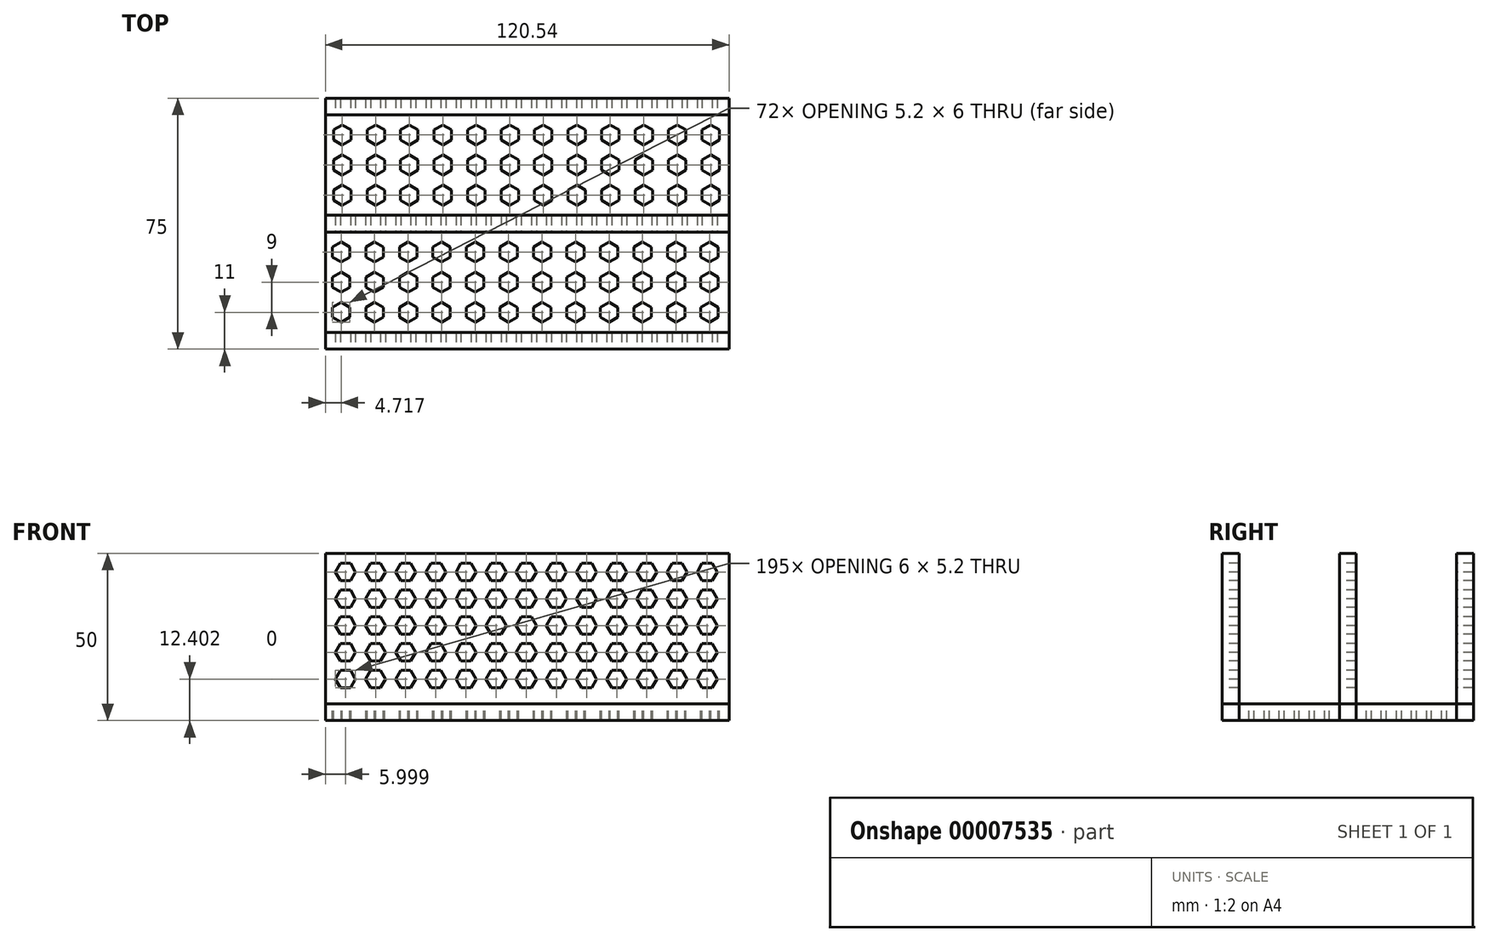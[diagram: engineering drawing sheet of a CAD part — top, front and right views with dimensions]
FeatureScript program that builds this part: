
annotation { "Feature Type Name" : "Feature", "Feature Type Description" : "" }
export const myFeature = defineFeature(function(context is Context, id is Id, definition is map)
    precondition{}
    {
        {
            var Q0;
            Q0=qCreatedBy(makeId("Top.planeOp"),FACE);
            var sketch = newSketch(context, id + "F0", { "sketchPlane" : qUnion([Q0])});
            skLineSegment(sketch, "E0.bottom", {"start": v(-52.44, 35) * mm, "end": v(68.1, 35) * mm});
            skLineSegment(sketch, "E0.top", {"start": v(-52.44, -40) * mm, "end": v(68.1, -40) * mm});
            skLineSegment(sketch, "E0.left", {"start": v(-52.44, 35) * mm, "end": v(-52.44, -40) * mm});
            skLineSegment(sketch, "E0.right", {"start": v(68.1, 35) * mm, "end": v(68.1, -40) * mm});
            skLineSegment(sketch, "E1.top", {"start": v(-52.44, -35) * mm, "end": v(68.1, -35) * mm});
            skLineSegment(sketch, "E1.left", {"start": v(-52.44, -40) * mm, "end": v(-52.44, -35) * mm});
            skLineSegment(sketch, "E1.right", {"start": v(68.1, -40) * mm, "end": v(68.1, -35) * mm});
            skLineSegment(sketch, "E2.bottom", {"start": v(68.1, -5) * mm, "end": v(-52.44, -5) * mm});
            skLineSegment(sketch, "E2.top", {"start": v(68.1, 0) * mm, "end": v(-52.44, 0) * mm});
            skLineSegment(sketch, "E2.left", {"start": v(68.1, -5) * mm, "end": v(68.1, 0) * mm});
            skLineSegment(sketch, "E2.right", {"start": v(-52.44, -5) * mm, "end": v(-52.44, 0) * mm});
            skLineSegment(sketch, "E3.top", {"start": v(-52.44, 30) * mm, "end": v(68.1, 30) * mm});
            skLineSegment(sketch, "E3.left", {"start": v(-52.44, 35) * mm, "end": v(-52.44, 30) * mm});
            skLineSegment(sketch, "E3.right", {"start": v(68.1, 35) * mm, "end": v(68.1, 30) * mm});
            skSolve(sketch);
        }
        {
            var Q0;
            Q0 = qSketchRegion(id + "F0", true);
            extrude(context, id + "F1", {"entities" : qUnion([Q0]), "depth" : 5 * mm});
        }
        {
            var Q0;
            Q0=makeQuery(id+"F0.imprint","IMPRINT",FACE,{"disambiguationData":[TD([[makeQuery(id+"F0.imprint","IMPRINT",EDGE,{"derivedFrom":sQuery(id+"F0.wireOp",EDGE,"E0.top")}),1.0]])]});
            var Q1;
            Q1=makeQuery(id+"F0.imprint","IMPRINT",FACE,{"disambiguationData":[TD([[makeQuery(id+"F0.imprint","IMPRINT",EDGE,{"derivedFrom":sQuery(id+"F0.wireOp",EDGE,"E2.bottom")}),-1.0]])]});
            var Q2;
            Q2=makeQuery(id+"F0.imprint","IMPRINT",FACE,{"disambiguationData":[TD([[makeQuery(id+"F0.imprint","IMPRINT",EDGE,{"derivedFrom":sQuery(id+"F0.wireOp",EDGE,"E0.bottom")}),-1.0]])]});
            extrude(context, id + "F2", {"entities" : qUnion([Q0, Q1, Q2]), "depth" : 50 * mm});
        }
        {
            var Q0;
            Q0=makeQuery(id+"F1.opExtrude","CAP_FACE",FACE,{"disambiguationData":[OSD([sQuery(id+"F0.wireOp",EDGE,"E0.left"),sQuery(id+"F0.wireOp",EDGE,"E0.right"),sQuery(id+"F0.wireOp",EDGE,"E0.top"),sQuery(id+"F0.wireOp",EDGE,"E1.left"),sQuery(id+"F0.wireOp",EDGE,"E1.right"),sQuery(id+"F0.wireOp",EDGE,"E2.left"),sQuery(id+"F0.wireOp",EDGE,"E2.right"),sQuery(id+"F0.wireOp",EDGE,"E0.bottom"),sQuery(id+"F0.wireOp",EDGE,"E3.left"),sQuery(id+"F0.wireOp",EDGE,"E3.right")])],"isStart":false});
            var sketch = newSketch(context, id + "F3", { "sketchPlane" : qUnion([Q0])});
            skCircle(sketch, "E4.cCircle", {"center": v(-47.37, 24) * mm, "radius": 2.6 * mm, "construction": true});
            skLineSegment(sketch, "E4.0", {"start": v(-49.97, 22.5) * mm, "end": v(-49.97, 25.5) * mm});
            skLineSegment(sketch, "E4.1", {"start": v(-49.97, 25.5) * mm, "end": v(-47.37, 27) * mm});
            skLineSegment(sketch, "E4.2", {"start": v(-47.37, 27) * mm, "end": v(-44.78, 25.5) * mm});
            skLineSegment(sketch, "E4.3", {"start": v(-44.78, 25.5) * mm, "end": v(-44.78, 22.5) * mm});
            skLineSegment(sketch, "E4.4", {"start": v(-44.78, 22.5) * mm, "end": v(-47.37, 21) * mm});
            skLineSegment(sketch, "E4.5", {"start": v(-47.37, 21) * mm, "end": v(-49.97, 22.5) * mm});
            skPoint(sketch, "E4.0.midPoint", {"position": v(-49.97, 24) * mm});
            skCircle(sketch, "E5.cCircle", {"center": v(-47.37, 15) * mm, "radius": 2.6 * mm, "construction": true});
            skLineSegment(sketch, "E5.0", {"start": v(-49.97, 13.5) * mm, "end": v(-49.97, 16.5) * mm});
            skLineSegment(sketch, "E5.1", {"start": v(-49.97, 16.5) * mm, "end": v(-47.37, 18) * mm});
            skLineSegment(sketch, "E5.2", {"start": v(-47.37, 18) * mm, "end": v(-44.78, 16.5) * mm});
            skLineSegment(sketch, "E5.3", {"start": v(-44.78, 16.5) * mm, "end": v(-44.78, 13.5) * mm});
            skLineSegment(sketch, "E5.4", {"start": v(-44.78, 13.5) * mm, "end": v(-47.37, 12) * mm});
            skLineSegment(sketch, "E5.5", {"start": v(-47.37, 12) * mm, "end": v(-49.97, 13.5) * mm});
            skPoint(sketch, "E5.0.midPoint", {"position": v(-49.97, 15) * mm});
            skCircle(sketch, "E6.cCircle", {"center": v(-47.37, 6) * mm, "radius": 2.6 * mm, "construction": true});
            skLineSegment(sketch, "E6.0", {"start": v(-49.97, 4.5) * mm, "end": v(-49.97, 7.5) * mm});
            skLineSegment(sketch, "E6.1", {"start": v(-49.97, 7.5) * mm, "end": v(-47.37, 9) * mm});
            skLineSegment(sketch, "E6.2", {"start": v(-47.37, 9) * mm, "end": v(-44.78, 7.5) * mm});
            skLineSegment(sketch, "E6.3", {"start": v(-44.78, 7.5) * mm, "end": v(-44.78, 4.5) * mm});
            skLineSegment(sketch, "E6.4", {"start": v(-44.78, 4.5) * mm, "end": v(-47.37, 3) * mm});
            skLineSegment(sketch, "E6.5", {"start": v(-47.37, 3) * mm, "end": v(-49.97, 4.5) * mm});
            skPoint(sketch, "E6.0.midPoint", {"position": v(-49.97, 6) * mm});
            skCircle(sketch, "E7.cCircle", {"center": v(-47.72, -11) * mm, "radius": 2.6 * mm, "construction": true});
            skLineSegment(sketch, "E7.0", {"start": v(-50.32, -12.5) * mm, "end": v(-50.32, -9.5) * mm});
            skLineSegment(sketch, "E7.1", {"start": v(-50.32, -9.5) * mm, "end": v(-47.72, -8) * mm});
            skLineSegment(sketch, "E7.2", {"start": v(-47.72, -8) * mm, "end": v(-45.13, -9.5) * mm});
            skLineSegment(sketch, "E7.3", {"start": v(-45.13, -9.5) * mm, "end": v(-45.13, -12.5) * mm});
            skLineSegment(sketch, "E7.4", {"start": v(-45.13, -12.5) * mm, "end": v(-47.72, -14) * mm});
            skLineSegment(sketch, "E7.5", {"start": v(-47.72, -14) * mm, "end": v(-50.32, -12.5) * mm});
            skPoint(sketch, "E7.0.midPoint", {"position": v(-50.32, -11) * mm});
            skCircle(sketch, "E8.cCircle", {"center": v(-47.72, -20) * mm, "radius": 2.6 * mm, "construction": true});
            skLineSegment(sketch, "E8.0", {"start": v(-50.32, -21.5) * mm, "end": v(-50.32, -18.5) * mm});
            skLineSegment(sketch, "E8.1", {"start": v(-50.32, -18.5) * mm, "end": v(-47.72, -17) * mm});
            skLineSegment(sketch, "E8.2", {"start": v(-47.72, -17) * mm, "end": v(-45.13, -18.5) * mm});
            skLineSegment(sketch, "E8.3", {"start": v(-45.13, -18.5) * mm, "end": v(-45.13, -21.5) * mm});
            skLineSegment(sketch, "E8.4", {"start": v(-45.13, -21.5) * mm, "end": v(-47.72, -23) * mm});
            skLineSegment(sketch, "E8.5", {"start": v(-47.72, -23) * mm, "end": v(-50.32, -21.5) * mm});
            skPoint(sketch, "E8.0.midPoint", {"position": v(-50.32, -20) * mm});
            skCircle(sketch, "E9.cCircle", {"center": v(-47.72, -29) * mm, "radius": 2.6 * mm, "construction": true});
            skLineSegment(sketch, "E9.0", {"start": v(-50.32, -30.5) * mm, "end": v(-50.32, -27.5) * mm});
            skLineSegment(sketch, "E9.1", {"start": v(-50.32, -27.5) * mm, "end": v(-47.72, -26) * mm});
            skLineSegment(sketch, "E9.2", {"start": v(-47.72, -26) * mm, "end": v(-45.13, -27.5) * mm});
            skLineSegment(sketch, "E9.3", {"start": v(-45.13, -27.5) * mm, "end": v(-45.13, -30.5) * mm});
            skLineSegment(sketch, "E9.4", {"start": v(-45.13, -30.5) * mm, "end": v(-47.72, -32) * mm});
            skLineSegment(sketch, "E9.5", {"start": v(-47.72, -32) * mm, "end": v(-50.32, -30.5) * mm});
            skPoint(sketch, "E9.0.midPoint", {"position": v(-50.32, -29) * mm});
            skPoint(sketch, "E10.1.0.0", {"position": v(-40.32, -29) * mm});
            skLineSegment(sketch, "E10.1.0.1", {"start": v(-40.32, -27.5) * mm, "end": v(-37.72, -26) * mm});
            skLineSegment(sketch, "E10.1.0.2", {"start": v(-37.72, -26) * mm, "end": v(-35.13, -27.5) * mm});
            skLineSegment(sketch, "E10.1.0.3", {"start": v(-40.32, -9.5) * mm, "end": v(-37.72, -8) * mm});
            skLineSegment(sketch, "E10.1.0.4", {"start": v(-35.13, -27.5) * mm, "end": v(-35.13, -30.5) * mm});
            skLineSegment(sketch, "E10.1.0.5", {"start": v(-35.13, -30.5) * mm, "end": v(-37.72, -32) * mm});
            skLineSegment(sketch, "E10.1.0.6", {"start": v(-37.72, -8) * mm, "end": v(-35.13, -9.5) * mm});
            skLineSegment(sketch, "E10.1.0.7", {"start": v(-37.72, -32) * mm, "end": v(-40.32, -30.5) * mm});
            skLineSegment(sketch, "E10.1.0.8", {"start": v(-35.13, -9.5) * mm, "end": v(-35.13, -12.5) * mm});
            skLineSegment(sketch, "E10.1.0.9", {"start": v(-37.37, 12) * mm, "end": v(-39.97, 13.5) * mm});
            skPoint(sketch, "E10.1.0.10", {"position": v(-39.97, 24) * mm});
            skLineSegment(sketch, "E10.1.0.11", {"start": v(-39.97, 16.5) * mm, "end": v(-37.37, 18) * mm});
            skLineSegment(sketch, "E10.1.0.12", {"start": v(-37.37, 18) * mm, "end": v(-34.78, 16.5) * mm});
            skLineSegment(sketch, "E10.1.0.13", {"start": v(-34.78, 16.5) * mm, "end": v(-34.78, 13.5) * mm});
            skLineSegment(sketch, "E10.1.0.14", {"start": v(-34.78, 13.5) * mm, "end": v(-37.37, 12) * mm});
            skLineSegment(sketch, "E10.1.0.15", {"start": v(-39.97, 25.5) * mm, "end": v(-37.37, 27) * mm});
            skLineSegment(sketch, "E10.1.0.16", {"start": v(-37.37, 27) * mm, "end": v(-34.78, 25.5) * mm});
            skLineSegment(sketch, "E10.1.0.17", {"start": v(-34.78, 25.5) * mm, "end": v(-34.78, 22.5) * mm});
            skLineSegment(sketch, "E10.1.0.18", {"start": v(-34.78, 22.5) * mm, "end": v(-37.37, 21) * mm});
            skLineSegment(sketch, "E10.1.0.19", {"start": v(-35.13, -12.5) * mm, "end": v(-37.72, -14) * mm});
            skLineSegment(sketch, "E10.1.0.20", {"start": v(-37.37, 21) * mm, "end": v(-39.97, 22.5) * mm});
            skLineSegment(sketch, "E10.1.0.21", {"start": v(-37.72, -14) * mm, "end": v(-40.32, -12.5) * mm});
            skPoint(sketch, "E10.1.0.22", {"position": v(-39.97, 15) * mm});
            skPoint(sketch, "E10.1.0.23", {"position": v(-39.97, 6) * mm});
            skLineSegment(sketch, "E10.1.0.24", {"start": v(-37.72, -17) * mm, "end": v(-35.13, -18.5) * mm});
            skPoint(sketch, "E10.1.0.25", {"position": v(-40.32, -11) * mm});
            skLineSegment(sketch, "E10.1.0.26", {"start": v(-40.32, -18.5) * mm, "end": v(-37.72, -17) * mm});
            skLineSegment(sketch, "E10.1.0.27", {"start": v(-39.97, 7.5) * mm, "end": v(-37.37, 9) * mm});
            skLineSegment(sketch, "E10.1.0.28", {"start": v(-35.13, -18.5) * mm, "end": v(-35.13, -21.5) * mm});
            skLineSegment(sketch, "E10.1.0.29", {"start": v(-37.72, -23) * mm, "end": v(-40.32, -21.5) * mm});
            skLineSegment(sketch, "E10.1.0.30", {"start": v(-34.78, 7.5) * mm, "end": v(-34.78, 4.5) * mm});
            skPoint(sketch, "E10.1.0.31", {"position": v(-40.32, -20) * mm});
            skLineSegment(sketch, "E10.1.0.32", {"start": v(-37.37, 9) * mm, "end": v(-34.78, 7.5) * mm});
            skLineSegment(sketch, "E10.1.0.33", {"start": v(-35.13, -21.5) * mm, "end": v(-37.72, -23) * mm});
            skLineSegment(sketch, "E10.1.0.34", {"start": v(-37.37, 3) * mm, "end": v(-39.97, 4.5) * mm});
            skLineSegment(sketch, "E10.1.0.35", {"start": v(-34.78, 4.5) * mm, "end": v(-37.37, 3) * mm});
            skCircle(sketch, "E10.1.0.36", {"center": v(-37.72, -29) * mm, "radius": 2.6 * mm, "construction": true});
            skCircle(sketch, "E10.1.0.37", {"center": v(-37.72, -11) * mm, "radius": 2.6 * mm, "construction": true});
            skLineSegment(sketch, "E10.1.0.38", {"start": v(-40.32, -12.5) * mm, "end": v(-40.32, -9.5) * mm});
            skLineSegment(sketch, "E10.1.0.39", {"start": v(-39.97, 4.5) * mm, "end": v(-39.97, 7.5) * mm});
            skCircle(sketch, "E10.1.0.40", {"center": v(-37.37, 6) * mm, "radius": 2.6 * mm, "construction": true});
            skCircle(sketch, "E10.1.0.41", {"center": v(-37.37, 15) * mm, "radius": 2.6 * mm, "construction": true});
            skLineSegment(sketch, "E10.1.0.42", {"start": v(-39.97, 13.5) * mm, "end": v(-39.97, 16.5) * mm});
            skCircle(sketch, "E10.1.0.43", {"center": v(-37.37, 24) * mm, "radius": 2.6 * mm, "construction": true});
            skLineSegment(sketch, "E10.1.0.44", {"start": v(-39.97, 22.5) * mm, "end": v(-39.97, 25.5) * mm});
            skCircle(sketch, "E10.1.0.45", {"center": v(-37.72, -20) * mm, "radius": 2.6 * mm, "construction": true});
            skLineSegment(sketch, "E10.1.0.46", {"start": v(-40.32, -21.5) * mm, "end": v(-40.32, -18.5) * mm});
            skLineSegment(sketch, "E10.1.0.47", {"start": v(-40.32, -30.5) * mm, "end": v(-40.32, -27.5) * mm});
            skPoint(sketch, "E10.2.0.0", {"position": v(-30.32, -29) * mm});
            skLineSegment(sketch, "E10.2.0.1", {"start": v(-30.32, -27.5) * mm, "end": v(-27.72, -26) * mm});
            skLineSegment(sketch, "E10.2.0.2", {"start": v(-27.72, -26) * mm, "end": v(-25.13, -27.5) * mm});
            skLineSegment(sketch, "E10.2.0.3", {"start": v(-30.32, -9.5) * mm, "end": v(-27.72, -8) * mm});
            skLineSegment(sketch, "E10.2.0.4", {"start": v(-25.13, -27.5) * mm, "end": v(-25.13, -30.5) * mm});
            skLineSegment(sketch, "E10.2.0.5", {"start": v(-25.13, -30.5) * mm, "end": v(-27.72, -32) * mm});
            skLineSegment(sketch, "E10.2.0.6", {"start": v(-27.72, -8) * mm, "end": v(-25.13, -9.5) * mm});
            skLineSegment(sketch, "E10.2.0.7", {"start": v(-27.72, -32) * mm, "end": v(-30.32, -30.5) * mm});
            skLineSegment(sketch, "E10.2.0.8", {"start": v(-25.13, -9.5) * mm, "end": v(-25.13, -12.5) * mm});
            skLineSegment(sketch, "E10.2.0.9", {"start": v(-27.37, 12) * mm, "end": v(-29.97, 13.5) * mm});
            skPoint(sketch, "E10.2.0.10", {"position": v(-29.97, 24) * mm});
            skLineSegment(sketch, "E10.2.0.11", {"start": v(-29.97, 16.5) * mm, "end": v(-27.37, 18) * mm});
            skLineSegment(sketch, "E10.2.0.12", {"start": v(-27.37, 18) * mm, "end": v(-24.78, 16.5) * mm});
            skLineSegment(sketch, "E10.2.0.13", {"start": v(-24.78, 16.5) * mm, "end": v(-24.78, 13.5) * mm});
            skLineSegment(sketch, "E10.2.0.14", {"start": v(-24.78, 13.5) * mm, "end": v(-27.37, 12) * mm});
            skLineSegment(sketch, "E10.2.0.15", {"start": v(-29.97, 25.5) * mm, "end": v(-27.37, 27) * mm});
            skLineSegment(sketch, "E10.2.0.16", {"start": v(-27.37, 27) * mm, "end": v(-24.78, 25.5) * mm});
            skLineSegment(sketch, "E10.2.0.17", {"start": v(-24.78, 25.5) * mm, "end": v(-24.78, 22.5) * mm});
            skLineSegment(sketch, "E10.2.0.18", {"start": v(-24.78, 22.5) * mm, "end": v(-27.37, 21) * mm});
            skLineSegment(sketch, "E10.2.0.19", {"start": v(-25.13, -12.5) * mm, "end": v(-27.72, -14) * mm});
            skLineSegment(sketch, "E10.2.0.20", {"start": v(-27.37, 21) * mm, "end": v(-29.97, 22.5) * mm});
            skLineSegment(sketch, "E10.2.0.21", {"start": v(-27.72, -14) * mm, "end": v(-30.32, -12.5) * mm});
            skPoint(sketch, "E10.2.0.22", {"position": v(-29.97, 15) * mm});
            skPoint(sketch, "E10.2.0.23", {"position": v(-29.97, 6) * mm});
            skLineSegment(sketch, "E10.2.0.24", {"start": v(-27.72, -17) * mm, "end": v(-25.13, -18.5) * mm});
            skPoint(sketch, "E10.2.0.25", {"position": v(-30.32, -11) * mm});
            skLineSegment(sketch, "E10.2.0.26", {"start": v(-30.32, -18.5) * mm, "end": v(-27.72, -17) * mm});
            skLineSegment(sketch, "E10.2.0.27", {"start": v(-29.97, 7.5) * mm, "end": v(-27.37, 9) * mm});
            skLineSegment(sketch, "E10.2.0.28", {"start": v(-25.13, -18.5) * mm, "end": v(-25.13, -21.5) * mm});
            skLineSegment(sketch, "E10.2.0.29", {"start": v(-27.72, -23) * mm, "end": v(-30.32, -21.5) * mm});
            skLineSegment(sketch, "E10.2.0.30", {"start": v(-24.78, 7.5) * mm, "end": v(-24.78, 4.5) * mm});
            skPoint(sketch, "E10.2.0.31", {"position": v(-30.32, -20) * mm});
            skLineSegment(sketch, "E10.2.0.32", {"start": v(-27.37, 9) * mm, "end": v(-24.78, 7.5) * mm});
            skLineSegment(sketch, "E10.2.0.33", {"start": v(-25.13, -21.5) * mm, "end": v(-27.72, -23) * mm});
            skLineSegment(sketch, "E10.2.0.34", {"start": v(-27.37, 3) * mm, "end": v(-29.97, 4.5) * mm});
            skLineSegment(sketch, "E10.2.0.35", {"start": v(-24.78, 4.5) * mm, "end": v(-27.37, 3) * mm});
            skCircle(sketch, "E10.2.0.36", {"center": v(-27.72, -29) * mm, "radius": 2.6 * mm, "construction": true});
            skCircle(sketch, "E10.2.0.37", {"center": v(-27.72, -11) * mm, "radius": 2.6 * mm, "construction": true});
            skLineSegment(sketch, "E10.2.0.38", {"start": v(-30.32, -12.5) * mm, "end": v(-30.32, -9.5) * mm});
            skLineSegment(sketch, "E10.2.0.39", {"start": v(-29.97, 4.5) * mm, "end": v(-29.97, 7.5) * mm});
            skCircle(sketch, "E10.2.0.40", {"center": v(-27.37, 6) * mm, "radius": 2.6 * mm, "construction": true});
            skCircle(sketch, "E10.2.0.41", {"center": v(-27.37, 15) * mm, "radius": 2.6 * mm, "construction": true});
            skLineSegment(sketch, "E10.2.0.42", {"start": v(-29.97, 13.5) * mm, "end": v(-29.97, 16.5) * mm});
            skCircle(sketch, "E10.2.0.43", {"center": v(-27.37, 24) * mm, "radius": 2.6 * mm, "construction": true});
            skLineSegment(sketch, "E10.2.0.44", {"start": v(-29.97, 22.5) * mm, "end": v(-29.97, 25.5) * mm});
            skCircle(sketch, "E10.2.0.45", {"center": v(-27.72, -20) * mm, "radius": 2.6 * mm, "construction": true});
            skLineSegment(sketch, "E10.2.0.46", {"start": v(-30.32, -21.5) * mm, "end": v(-30.32, -18.5) * mm});
            skLineSegment(sketch, "E10.2.0.47", {"start": v(-30.32, -30.5) * mm, "end": v(-30.32, -27.5) * mm});
            skPoint(sketch, "E10.3.0.0", {"position": v(-20.32, -29) * mm});
            skLineSegment(sketch, "E10.3.0.1", {"start": v(-20.32, -27.5) * mm, "end": v(-17.72, -26) * mm});
            skLineSegment(sketch, "E10.3.0.2", {"start": v(-17.72, -26) * mm, "end": v(-15.13, -27.5) * mm});
            skLineSegment(sketch, "E10.3.0.3", {"start": v(-20.32, -9.5) * mm, "end": v(-17.72, -8) * mm});
            skLineSegment(sketch, "E10.3.0.4", {"start": v(-15.13, -27.5) * mm, "end": v(-15.13, -30.5) * mm});
            skLineSegment(sketch, "E10.3.0.5", {"start": v(-15.13, -30.5) * mm, "end": v(-17.72, -32) * mm});
            skLineSegment(sketch, "E10.3.0.6", {"start": v(-17.72, -8) * mm, "end": v(-15.13, -9.5) * mm});
            skLineSegment(sketch, "E10.3.0.7", {"start": v(-17.72, -32) * mm, "end": v(-20.32, -30.5) * mm});
            skLineSegment(sketch, "E10.3.0.8", {"start": v(-15.13, -9.5) * mm, "end": v(-15.13, -12.5) * mm});
            skLineSegment(sketch, "E10.3.0.9", {"start": v(-17.37, 12) * mm, "end": v(-19.97, 13.5) * mm});
            skPoint(sketch, "E10.3.0.10", {"position": v(-19.97, 24) * mm});
            skLineSegment(sketch, "E10.3.0.11", {"start": v(-19.97, 16.5) * mm, "end": v(-17.37, 18) * mm});
            skLineSegment(sketch, "E10.3.0.12", {"start": v(-17.37, 18) * mm, "end": v(-14.78, 16.5) * mm});
            skLineSegment(sketch, "E10.3.0.13", {"start": v(-14.78, 16.5) * mm, "end": v(-14.78, 13.5) * mm});
            skLineSegment(sketch, "E10.3.0.14", {"start": v(-14.78, 13.5) * mm, "end": v(-17.37, 12) * mm});
            skLineSegment(sketch, "E10.3.0.15", {"start": v(-19.97, 25.5) * mm, "end": v(-17.37, 27) * mm});
            skLineSegment(sketch, "E10.3.0.16", {"start": v(-17.37, 27) * mm, "end": v(-14.78, 25.5) * mm});
            skLineSegment(sketch, "E10.3.0.17", {"start": v(-14.78, 25.5) * mm, "end": v(-14.78, 22.5) * mm});
            skLineSegment(sketch, "E10.3.0.18", {"start": v(-14.78, 22.5) * mm, "end": v(-17.37, 21) * mm});
            skLineSegment(sketch, "E10.3.0.19", {"start": v(-15.13, -12.5) * mm, "end": v(-17.72, -14) * mm});
            skLineSegment(sketch, "E10.3.0.20", {"start": v(-17.37, 21) * mm, "end": v(-19.97, 22.5) * mm});
            skLineSegment(sketch, "E10.3.0.21", {"start": v(-17.72, -14) * mm, "end": v(-20.32, -12.5) * mm});
            skPoint(sketch, "E10.3.0.22", {"position": v(-19.97, 15) * mm});
            skPoint(sketch, "E10.3.0.23", {"position": v(-19.97, 6) * mm});
            skLineSegment(sketch, "E10.3.0.24", {"start": v(-17.72, -17) * mm, "end": v(-15.13, -18.5) * mm});
            skPoint(sketch, "E10.3.0.25", {"position": v(-20.32, -11) * mm});
            skLineSegment(sketch, "E10.3.0.26", {"start": v(-20.32, -18.5) * mm, "end": v(-17.72, -17) * mm});
            skLineSegment(sketch, "E10.3.0.27", {"start": v(-19.97, 7.5) * mm, "end": v(-17.37, 9) * mm});
            skLineSegment(sketch, "E10.3.0.28", {"start": v(-15.13, -18.5) * mm, "end": v(-15.13, -21.5) * mm});
            skLineSegment(sketch, "E10.3.0.29", {"start": v(-17.72, -23) * mm, "end": v(-20.32, -21.5) * mm});
            skLineSegment(sketch, "E10.3.0.30", {"start": v(-14.78, 7.5) * mm, "end": v(-14.78, 4.5) * mm});
            skPoint(sketch, "E10.3.0.31", {"position": v(-20.32, -20) * mm});
            skLineSegment(sketch, "E10.3.0.32", {"start": v(-17.37, 9) * mm, "end": v(-14.78, 7.5) * mm});
            skLineSegment(sketch, "E10.3.0.33", {"start": v(-15.13, -21.5) * mm, "end": v(-17.72, -23) * mm});
            skLineSegment(sketch, "E10.3.0.34", {"start": v(-17.37, 3) * mm, "end": v(-19.97, 4.5) * mm});
            skLineSegment(sketch, "E10.3.0.35", {"start": v(-14.78, 4.5) * mm, "end": v(-17.37, 3) * mm});
            skCircle(sketch, "E10.3.0.36", {"center": v(-17.72, -29) * mm, "radius": 2.6 * mm, "construction": true});
            skCircle(sketch, "E10.3.0.37", {"center": v(-17.72, -11) * mm, "radius": 2.6 * mm, "construction": true});
            skLineSegment(sketch, "E10.3.0.38", {"start": v(-20.32, -12.5) * mm, "end": v(-20.32, -9.5) * mm});
            skLineSegment(sketch, "E10.3.0.39", {"start": v(-19.97, 4.5) * mm, "end": v(-19.97, 7.5) * mm});
            skCircle(sketch, "E10.3.0.40", {"center": v(-17.37, 6) * mm, "radius": 2.6 * mm, "construction": true});
            skCircle(sketch, "E10.3.0.41", {"center": v(-17.37, 15) * mm, "radius": 2.6 * mm, "construction": true});
            skLineSegment(sketch, "E10.3.0.42", {"start": v(-19.97, 13.5) * mm, "end": v(-19.97, 16.5) * mm});
            skCircle(sketch, "E10.3.0.43", {"center": v(-17.37, 24) * mm, "radius": 2.6 * mm, "construction": true});
            skLineSegment(sketch, "E10.3.0.44", {"start": v(-19.97, 22.5) * mm, "end": v(-19.97, 25.5) * mm});
            skCircle(sketch, "E10.3.0.45", {"center": v(-17.72, -20) * mm, "radius": 2.6 * mm, "construction": true});
            skLineSegment(sketch, "E10.3.0.46", {"start": v(-20.32, -21.5) * mm, "end": v(-20.32, -18.5) * mm});
            skLineSegment(sketch, "E10.3.0.47", {"start": v(-20.32, -30.5) * mm, "end": v(-20.32, -27.5) * mm});
            skPoint(sketch, "E10.4.0.0", {"position": v(-10.32, -29) * mm});
            skLineSegment(sketch, "E10.4.0.1", {"start": v(-10.32, -27.5) * mm, "end": v(-7.72, -26) * mm});
            skLineSegment(sketch, "E10.4.0.2", {"start": v(-7.72, -26) * mm, "end": v(-5.13, -27.5) * mm});
            skLineSegment(sketch, "E10.4.0.3", {"start": v(-10.32, -9.5) * mm, "end": v(-7.72, -8) * mm});
            skLineSegment(sketch, "E10.4.0.4", {"start": v(-5.13, -27.5) * mm, "end": v(-5.13, -30.5) * mm});
            skLineSegment(sketch, "E10.4.0.5", {"start": v(-5.13, -30.5) * mm, "end": v(-7.72, -32) * mm});
            skLineSegment(sketch, "E10.4.0.6", {"start": v(-7.72, -8) * mm, "end": v(-5.13, -9.5) * mm});
            skLineSegment(sketch, "E10.4.0.7", {"start": v(-7.72, -32) * mm, "end": v(-10.32, -30.5) * mm});
            skLineSegment(sketch, "E10.4.0.8", {"start": v(-5.13, -9.5) * mm, "end": v(-5.13, -12.5) * mm});
            skLineSegment(sketch, "E10.4.0.9", {"start": v(-7.37, 12) * mm, "end": v(-9.97, 13.5) * mm});
            skPoint(sketch, "E10.4.0.10", {"position": v(-9.97, 24) * mm});
            skLineSegment(sketch, "E10.4.0.11", {"start": v(-9.97, 16.5) * mm, "end": v(-7.37, 18) * mm});
            skLineSegment(sketch, "E10.4.0.12", {"start": v(-7.37, 18) * mm, "end": v(-4.78, 16.5) * mm});
            skLineSegment(sketch, "E10.4.0.13", {"start": v(-4.78, 16.5) * mm, "end": v(-4.78, 13.5) * mm});
            skLineSegment(sketch, "E10.4.0.14", {"start": v(-4.78, 13.5) * mm, "end": v(-7.37, 12) * mm});
            skLineSegment(sketch, "E10.4.0.15", {"start": v(-9.97, 25.5) * mm, "end": v(-7.37, 27) * mm});
            skLineSegment(sketch, "E10.4.0.16", {"start": v(-7.37, 27) * mm, "end": v(-4.78, 25.5) * mm});
            skLineSegment(sketch, "E10.4.0.17", {"start": v(-4.78, 25.5) * mm, "end": v(-4.78, 22.5) * mm});
            skLineSegment(sketch, "E10.4.0.18", {"start": v(-4.78, 22.5) * mm, "end": v(-7.37, 21) * mm});
            skLineSegment(sketch, "E10.4.0.19", {"start": v(-5.13, -12.5) * mm, "end": v(-7.72, -14) * mm});
            skLineSegment(sketch, "E10.4.0.20", {"start": v(-7.37, 21) * mm, "end": v(-9.97, 22.5) * mm});
            skLineSegment(sketch, "E10.4.0.21", {"start": v(-7.72, -14) * mm, "end": v(-10.32, -12.5) * mm});
            skPoint(sketch, "E10.4.0.22", {"position": v(-9.97, 15) * mm});
            skPoint(sketch, "E10.4.0.23", {"position": v(-9.97, 6) * mm});
            skLineSegment(sketch, "E10.4.0.24", {"start": v(-7.72, -17) * mm, "end": v(-5.13, -18.5) * mm});
            skPoint(sketch, "E10.4.0.25", {"position": v(-10.32, -11) * mm});
            skLineSegment(sketch, "E10.4.0.26", {"start": v(-10.32, -18.5) * mm, "end": v(-7.72, -17) * mm});
            skLineSegment(sketch, "E10.4.0.27", {"start": v(-9.97, 7.5) * mm, "end": v(-7.37, 9) * mm});
            skLineSegment(sketch, "E10.4.0.28", {"start": v(-5.13, -18.5) * mm, "end": v(-5.13, -21.5) * mm});
            skLineSegment(sketch, "E10.4.0.29", {"start": v(-7.72, -23) * mm, "end": v(-10.32, -21.5) * mm});
            skLineSegment(sketch, "E10.4.0.30", {"start": v(-4.78, 7.5) * mm, "end": v(-4.78, 4.5) * mm});
            skPoint(sketch, "E10.4.0.31", {"position": v(-10.32, -20) * mm});
            skLineSegment(sketch, "E10.4.0.32", {"start": v(-7.37, 9) * mm, "end": v(-4.78, 7.5) * mm});
            skLineSegment(sketch, "E10.4.0.33", {"start": v(-5.13, -21.5) * mm, "end": v(-7.72, -23) * mm});
            skLineSegment(sketch, "E10.4.0.34", {"start": v(-7.37, 3) * mm, "end": v(-9.97, 4.5) * mm});
            skLineSegment(sketch, "E10.4.0.35", {"start": v(-4.78, 4.5) * mm, "end": v(-7.37, 3) * mm});
            skCircle(sketch, "E10.4.0.36", {"center": v(-7.72, -29) * mm, "radius": 2.6 * mm, "construction": true});
            skCircle(sketch, "E10.4.0.37", {"center": v(-7.72, -11) * mm, "radius": 2.6 * mm, "construction": true});
            skLineSegment(sketch, "E10.4.0.38", {"start": v(-10.32, -12.5) * mm, "end": v(-10.32, -9.5) * mm});
            skLineSegment(sketch, "E10.4.0.39", {"start": v(-9.97, 4.5) * mm, "end": v(-9.97, 7.5) * mm});
            skCircle(sketch, "E10.4.0.40", {"center": v(-7.37, 6) * mm, "radius": 2.6 * mm, "construction": true});
            skCircle(sketch, "E10.4.0.41", {"center": v(-7.37, 15) * mm, "radius": 2.6 * mm, "construction": true});
            skLineSegment(sketch, "E10.4.0.42", {"start": v(-9.97, 13.5) * mm, "end": v(-9.97, 16.5) * mm});
            skCircle(sketch, "E10.4.0.43", {"center": v(-7.37, 24) * mm, "radius": 2.6 * mm, "construction": true});
            skLineSegment(sketch, "E10.4.0.44", {"start": v(-9.97, 22.5) * mm, "end": v(-9.97, 25.5) * mm});
            skCircle(sketch, "E10.4.0.45", {"center": v(-7.72, -20) * mm, "radius": 2.6 * mm, "construction": true});
            skLineSegment(sketch, "E10.4.0.46", {"start": v(-10.32, -21.5) * mm, "end": v(-10.32, -18.5) * mm});
            skLineSegment(sketch, "E10.4.0.47", {"start": v(-10.32, -30.5) * mm, "end": v(-10.32, -27.5) * mm});
            skPoint(sketch, "E10.5.0.0", {"position": v(-0.32, -29) * mm});
            skLineSegment(sketch, "E10.5.0.1", {"start": v(-0.32, -27.5) * mm, "end": v(2.28, -26) * mm});
            skLineSegment(sketch, "E10.5.0.2", {"start": v(2.28, -26) * mm, "end": v(4.87, -27.5) * mm});
            skLineSegment(sketch, "E10.5.0.3", {"start": v(-0.32, -9.5) * mm, "end": v(2.28, -8) * mm});
            skLineSegment(sketch, "E10.5.0.4", {"start": v(4.87, -27.5) * mm, "end": v(4.87, -30.5) * mm});
            skLineSegment(sketch, "E10.5.0.5", {"start": v(4.87, -30.5) * mm, "end": v(2.28, -32) * mm});
            skLineSegment(sketch, "E10.5.0.6", {"start": v(2.28, -8) * mm, "end": v(4.87, -9.5) * mm});
            skLineSegment(sketch, "E10.5.0.7", {"start": v(2.28, -32) * mm, "end": v(-0.32, -30.5) * mm});
            skLineSegment(sketch, "E10.5.0.8", {"start": v(4.87, -9.5) * mm, "end": v(4.87, -12.5) * mm});
            skLineSegment(sketch, "E10.5.0.9", {"start": v(2.63, 12) * mm, "end": v(0.03, 13.5) * mm});
            skPoint(sketch, "E10.5.0.10", {"position": v(0.03, 24) * mm});
            skLineSegment(sketch, "E10.5.0.11", {"start": v(0.03, 16.5) * mm, "end": v(2.63, 18) * mm});
            skLineSegment(sketch, "E10.5.0.12", {"start": v(2.63, 18) * mm, "end": v(5.22, 16.5) * mm});
            skLineSegment(sketch, "E10.5.0.13", {"start": v(5.22, 16.5) * mm, "end": v(5.22, 13.5) * mm});
            skLineSegment(sketch, "E10.5.0.14", {"start": v(5.22, 13.5) * mm, "end": v(2.63, 12) * mm});
            skLineSegment(sketch, "E10.5.0.15", {"start": v(0.03, 25.5) * mm, "end": v(2.63, 27) * mm});
            skLineSegment(sketch, "E10.5.0.16", {"start": v(2.63, 27) * mm, "end": v(5.22, 25.5) * mm});
            skLineSegment(sketch, "E10.5.0.17", {"start": v(5.22, 25.5) * mm, "end": v(5.22, 22.5) * mm});
            skLineSegment(sketch, "E10.5.0.18", {"start": v(5.22, 22.5) * mm, "end": v(2.63, 21) * mm});
            skLineSegment(sketch, "E10.5.0.19", {"start": v(4.87, -12.5) * mm, "end": v(2.28, -14) * mm});
            skLineSegment(sketch, "E10.5.0.20", {"start": v(2.63, 21) * mm, "end": v(0.03, 22.5) * mm});
            skLineSegment(sketch, "E10.5.0.21", {"start": v(2.28, -14) * mm, "end": v(-0.32, -12.5) * mm});
            skPoint(sketch, "E10.5.0.22", {"position": v(0.03, 15) * mm});
            skPoint(sketch, "E10.5.0.23", {"position": v(0.03, 6) * mm});
            skLineSegment(sketch, "E10.5.0.24", {"start": v(2.28, -17) * mm, "end": v(4.87, -18.5) * mm});
            skPoint(sketch, "E10.5.0.25", {"position": v(-0.32, -11) * mm});
            skLineSegment(sketch, "E10.5.0.26", {"start": v(-0.32, -18.5) * mm, "end": v(2.28, -17) * mm});
            skLineSegment(sketch, "E10.5.0.27", {"start": v(0.03, 7.5) * mm, "end": v(2.63, 9) * mm});
            skLineSegment(sketch, "E10.5.0.28", {"start": v(4.87, -18.5) * mm, "end": v(4.87, -21.5) * mm});
            skLineSegment(sketch, "E10.5.0.29", {"start": v(2.28, -23) * mm, "end": v(-0.32, -21.5) * mm});
            skLineSegment(sketch, "E10.5.0.30", {"start": v(5.22, 7.5) * mm, "end": v(5.22, 4.5) * mm});
            skPoint(sketch, "E10.5.0.31", {"position": v(-0.32, -20) * mm});
            skLineSegment(sketch, "E10.5.0.32", {"start": v(2.63, 9) * mm, "end": v(5.22, 7.5) * mm});
            skLineSegment(sketch, "E10.5.0.33", {"start": v(4.87, -21.5) * mm, "end": v(2.28, -23) * mm});
            skLineSegment(sketch, "E10.5.0.34", {"start": v(2.63, 3) * mm, "end": v(0.03, 4.5) * mm});
            skLineSegment(sketch, "E10.5.0.35", {"start": v(5.22, 4.5) * mm, "end": v(2.63, 3) * mm});
            skCircle(sketch, "E10.5.0.36", {"center": v(2.28, -29) * mm, "radius": 2.6 * mm, "construction": true});
            skCircle(sketch, "E10.5.0.37", {"center": v(2.28, -11) * mm, "radius": 2.6 * mm, "construction": true});
            skLineSegment(sketch, "E10.5.0.38", {"start": v(-0.32, -12.5) * mm, "end": v(-0.32, -9.5) * mm});
            skLineSegment(sketch, "E10.5.0.39", {"start": v(0.03, 4.5) * mm, "end": v(0.03, 7.5) * mm});
            skCircle(sketch, "E10.5.0.40", {"center": v(2.63, 6) * mm, "radius": 2.6 * mm, "construction": true});
            skCircle(sketch, "E10.5.0.41", {"center": v(2.63, 15) * mm, "radius": 2.6 * mm, "construction": true});
            skLineSegment(sketch, "E10.5.0.42", {"start": v(0.03, 13.5) * mm, "end": v(0.03, 16.5) * mm});
            skCircle(sketch, "E10.5.0.43", {"center": v(2.63, 24) * mm, "radius": 2.6 * mm, "construction": true});
            skLineSegment(sketch, "E10.5.0.44", {"start": v(0.03, 22.5) * mm, "end": v(0.03, 25.5) * mm});
            skCircle(sketch, "E10.5.0.45", {"center": v(2.28, -20) * mm, "radius": 2.6 * mm, "construction": true});
            skLineSegment(sketch, "E10.5.0.46", {"start": v(-0.32, -21.5) * mm, "end": v(-0.32, -18.5) * mm});
            skLineSegment(sketch, "E10.5.0.47", {"start": v(-0.32, -30.5) * mm, "end": v(-0.32, -27.5) * mm});
            skPoint(sketch, "E10.6.0.0", {"position": v(9.68, -29) * mm});
            skLineSegment(sketch, "E10.6.0.1", {"start": v(9.68, -27.5) * mm, "end": v(12.28, -26) * mm});
            skLineSegment(sketch, "E10.6.0.2", {"start": v(12.28, -26) * mm, "end": v(14.87, -27.5) * mm});
            skLineSegment(sketch, "E10.6.0.3", {"start": v(9.68, -9.5) * mm, "end": v(12.28, -8) * mm});
            skLineSegment(sketch, "E10.6.0.4", {"start": v(14.87, -27.5) * mm, "end": v(14.87, -30.5) * mm});
            skLineSegment(sketch, "E10.6.0.5", {"start": v(14.87, -30.5) * mm, "end": v(12.28, -32) * mm});
            skLineSegment(sketch, "E10.6.0.6", {"start": v(12.28, -8) * mm, "end": v(14.87, -9.5) * mm});
            skLineSegment(sketch, "E10.6.0.7", {"start": v(12.28, -32) * mm, "end": v(9.68, -30.5) * mm});
            skLineSegment(sketch, "E10.6.0.8", {"start": v(14.87, -9.5) * mm, "end": v(14.87, -12.5) * mm});
            skLineSegment(sketch, "E10.6.0.9", {"start": v(12.63, 12) * mm, "end": v(10.03, 13.5) * mm});
            skPoint(sketch, "E10.6.0.10", {"position": v(10.03, 24) * mm});
            skLineSegment(sketch, "E10.6.0.11", {"start": v(10.03, 16.5) * mm, "end": v(12.63, 18) * mm});
            skLineSegment(sketch, "E10.6.0.12", {"start": v(12.63, 18) * mm, "end": v(15.22, 16.5) * mm});
            skLineSegment(sketch, "E10.6.0.13", {"start": v(15.22, 16.5) * mm, "end": v(15.22, 13.5) * mm});
            skLineSegment(sketch, "E10.6.0.14", {"start": v(15.22, 13.5) * mm, "end": v(12.63, 12) * mm});
            skLineSegment(sketch, "E10.6.0.15", {"start": v(10.03, 25.5) * mm, "end": v(12.63, 27) * mm});
            skLineSegment(sketch, "E10.6.0.16", {"start": v(12.63, 27) * mm, "end": v(15.22, 25.5) * mm});
            skLineSegment(sketch, "E10.6.0.17", {"start": v(15.22, 25.5) * mm, "end": v(15.22, 22.5) * mm});
            skLineSegment(sketch, "E10.6.0.18", {"start": v(15.22, 22.5) * mm, "end": v(12.63, 21) * mm});
            skLineSegment(sketch, "E10.6.0.19", {"start": v(14.87, -12.5) * mm, "end": v(12.28, -14) * mm});
            skLineSegment(sketch, "E10.6.0.20", {"start": v(12.63, 21) * mm, "end": v(10.03, 22.5) * mm});
            skLineSegment(sketch, "E10.6.0.21", {"start": v(12.28, -14) * mm, "end": v(9.68, -12.5) * mm});
            skPoint(sketch, "E10.6.0.22", {"position": v(10.03, 15) * mm});
            skPoint(sketch, "E10.6.0.23", {"position": v(10.03, 6) * mm});
            skLineSegment(sketch, "E10.6.0.24", {"start": v(12.28, -17) * mm, "end": v(14.87, -18.5) * mm});
            skPoint(sketch, "E10.6.0.25", {"position": v(9.68, -11) * mm});
            skLineSegment(sketch, "E10.6.0.26", {"start": v(9.68, -18.5) * mm, "end": v(12.28, -17) * mm});
            skLineSegment(sketch, "E10.6.0.27", {"start": v(10.03, 7.5) * mm, "end": v(12.63, 9) * mm});
            skLineSegment(sketch, "E10.6.0.28", {"start": v(14.87, -18.5) * mm, "end": v(14.87, -21.5) * mm});
            skLineSegment(sketch, "E10.6.0.29", {"start": v(12.28, -23) * mm, "end": v(9.68, -21.5) * mm});
            skLineSegment(sketch, "E10.6.0.30", {"start": v(15.22, 7.5) * mm, "end": v(15.22, 4.5) * mm});
            skPoint(sketch, "E10.6.0.31", {"position": v(9.68, -20) * mm});
            skLineSegment(sketch, "E10.6.0.32", {"start": v(12.63, 9) * mm, "end": v(15.22, 7.5) * mm});
            skLineSegment(sketch, "E10.6.0.33", {"start": v(14.87, -21.5) * mm, "end": v(12.28, -23) * mm});
            skLineSegment(sketch, "E10.6.0.34", {"start": v(12.63, 3) * mm, "end": v(10.03, 4.5) * mm});
            skLineSegment(sketch, "E10.6.0.35", {"start": v(15.22, 4.5) * mm, "end": v(12.63, 3) * mm});
            skCircle(sketch, "E10.6.0.36", {"center": v(12.28, -29) * mm, "radius": 2.6 * mm, "construction": true});
            skCircle(sketch, "E10.6.0.37", {"center": v(12.28, -11) * mm, "radius": 2.6 * mm, "construction": true});
            skLineSegment(sketch, "E10.6.0.38", {"start": v(9.68, -12.5) * mm, "end": v(9.68, -9.5) * mm});
            skLineSegment(sketch, "E10.6.0.39", {"start": v(10.03, 4.5) * mm, "end": v(10.03, 7.5) * mm});
            skCircle(sketch, "E10.6.0.40", {"center": v(12.63, 6) * mm, "radius": 2.6 * mm, "construction": true});
            skCircle(sketch, "E10.6.0.41", {"center": v(12.63, 15) * mm, "radius": 2.6 * mm, "construction": true});
            skLineSegment(sketch, "E10.6.0.42", {"start": v(10.03, 13.5) * mm, "end": v(10.03, 16.5) * mm});
            skCircle(sketch, "E10.6.0.43", {"center": v(12.63, 24) * mm, "radius": 2.6 * mm, "construction": true});
            skLineSegment(sketch, "E10.6.0.44", {"start": v(10.03, 22.5) * mm, "end": v(10.03, 25.5) * mm});
            skCircle(sketch, "E10.6.0.45", {"center": v(12.28, -20) * mm, "radius": 2.6 * mm, "construction": true});
            skLineSegment(sketch, "E10.6.0.46", {"start": v(9.68, -21.5) * mm, "end": v(9.68, -18.5) * mm});
            skLineSegment(sketch, "E10.6.0.47", {"start": v(9.68, -30.5) * mm, "end": v(9.68, -27.5) * mm});
            skPoint(sketch, "E10.7.0.0", {"position": v(19.68, -29) * mm});
            skLineSegment(sketch, "E10.7.0.1", {"start": v(19.68, -27.5) * mm, "end": v(22.28, -26) * mm});
            skLineSegment(sketch, "E10.7.0.2", {"start": v(22.28, -26) * mm, "end": v(24.87, -27.5) * mm});
            skLineSegment(sketch, "E10.7.0.3", {"start": v(19.68, -9.5) * mm, "end": v(22.28, -8) * mm});
            skLineSegment(sketch, "E10.7.0.4", {"start": v(24.87, -27.5) * mm, "end": v(24.87, -30.5) * mm});
            skLineSegment(sketch, "E10.7.0.5", {"start": v(24.87, -30.5) * mm, "end": v(22.28, -32) * mm});
            skLineSegment(sketch, "E10.7.0.6", {"start": v(22.28, -8) * mm, "end": v(24.87, -9.5) * mm});
            skLineSegment(sketch, "E10.7.0.7", {"start": v(22.28, -32) * mm, "end": v(19.68, -30.5) * mm});
            skLineSegment(sketch, "E10.7.0.8", {"start": v(24.87, -9.5) * mm, "end": v(24.87, -12.5) * mm});
            skLineSegment(sketch, "E10.7.0.9", {"start": v(22.63, 12) * mm, "end": v(20.03, 13.5) * mm});
            skPoint(sketch, "E10.7.0.10", {"position": v(20.03, 24) * mm});
            skLineSegment(sketch, "E10.7.0.11", {"start": v(20.03, 16.5) * mm, "end": v(22.63, 18) * mm});
            skLineSegment(sketch, "E10.7.0.12", {"start": v(22.63, 18) * mm, "end": v(25.22, 16.5) * mm});
            skLineSegment(sketch, "E10.7.0.13", {"start": v(25.22, 16.5) * mm, "end": v(25.22, 13.5) * mm});
            skLineSegment(sketch, "E10.7.0.14", {"start": v(25.22, 13.5) * mm, "end": v(22.63, 12) * mm});
            skLineSegment(sketch, "E10.7.0.15", {"start": v(20.03, 25.5) * mm, "end": v(22.63, 27) * mm});
            skLineSegment(sketch, "E10.7.0.16", {"start": v(22.63, 27) * mm, "end": v(25.22, 25.5) * mm});
            skLineSegment(sketch, "E10.7.0.17", {"start": v(25.22, 25.5) * mm, "end": v(25.22, 22.5) * mm});
            skLineSegment(sketch, "E10.7.0.18", {"start": v(25.22, 22.5) * mm, "end": v(22.63, 21) * mm});
            skLineSegment(sketch, "E10.7.0.19", {"start": v(24.87, -12.5) * mm, "end": v(22.28, -14) * mm});
            skLineSegment(sketch, "E10.7.0.20", {"start": v(22.63, 21) * mm, "end": v(20.03, 22.5) * mm});
            skLineSegment(sketch, "E10.7.0.21", {"start": v(22.28, -14) * mm, "end": v(19.68, -12.5) * mm});
            skPoint(sketch, "E10.7.0.22", {"position": v(20.03, 15) * mm});
            skPoint(sketch, "E10.7.0.23", {"position": v(20.03, 6) * mm});
            skLineSegment(sketch, "E10.7.0.24", {"start": v(22.28, -17) * mm, "end": v(24.87, -18.5) * mm});
            skPoint(sketch, "E10.7.0.25", {"position": v(19.68, -11) * mm});
            skLineSegment(sketch, "E10.7.0.26", {"start": v(19.68, -18.5) * mm, "end": v(22.28, -17) * mm});
            skLineSegment(sketch, "E10.7.0.27", {"start": v(20.03, 7.5) * mm, "end": v(22.63, 9) * mm});
            skLineSegment(sketch, "E10.7.0.28", {"start": v(24.87, -18.5) * mm, "end": v(24.87, -21.5) * mm});
            skLineSegment(sketch, "E10.7.0.29", {"start": v(22.28, -23) * mm, "end": v(19.68, -21.5) * mm});
            skLineSegment(sketch, "E10.7.0.30", {"start": v(25.22, 7.5) * mm, "end": v(25.22, 4.5) * mm});
            skPoint(sketch, "E10.7.0.31", {"position": v(19.68, -20) * mm});
            skLineSegment(sketch, "E10.7.0.32", {"start": v(22.63, 9) * mm, "end": v(25.22, 7.5) * mm});
            skLineSegment(sketch, "E10.7.0.33", {"start": v(24.87, -21.5) * mm, "end": v(22.28, -23) * mm});
            skLineSegment(sketch, "E10.7.0.34", {"start": v(22.63, 3) * mm, "end": v(20.03, 4.5) * mm});
            skLineSegment(sketch, "E10.7.0.35", {"start": v(25.22, 4.5) * mm, "end": v(22.63, 3) * mm});
            skCircle(sketch, "E10.7.0.36", {"center": v(22.28, -29) * mm, "radius": 2.6 * mm, "construction": true});
            skCircle(sketch, "E10.7.0.37", {"center": v(22.28, -11) * mm, "radius": 2.6 * mm, "construction": true});
            skLineSegment(sketch, "E10.7.0.38", {"start": v(19.68, -12.5) * mm, "end": v(19.68, -9.5) * mm});
            skLineSegment(sketch, "E10.7.0.39", {"start": v(20.03, 4.5) * mm, "end": v(20.03, 7.5) * mm});
            skCircle(sketch, "E10.7.0.40", {"center": v(22.63, 6) * mm, "radius": 2.6 * mm, "construction": true});
            skCircle(sketch, "E10.7.0.41", {"center": v(22.63, 15) * mm, "radius": 2.6 * mm, "construction": true});
            skLineSegment(sketch, "E10.7.0.42", {"start": v(20.03, 13.5) * mm, "end": v(20.03, 16.5) * mm});
            skCircle(sketch, "E10.7.0.43", {"center": v(22.63, 24) * mm, "radius": 2.6 * mm, "construction": true});
            skLineSegment(sketch, "E10.7.0.44", {"start": v(20.03, 22.5) * mm, "end": v(20.03, 25.5) * mm});
            skCircle(sketch, "E10.7.0.45", {"center": v(22.28, -20) * mm, "radius": 2.6 * mm, "construction": true});
            skLineSegment(sketch, "E10.7.0.46", {"start": v(19.68, -21.5) * mm, "end": v(19.68, -18.5) * mm});
            skLineSegment(sketch, "E10.7.0.47", {"start": v(19.68, -30.5) * mm, "end": v(19.68, -27.5) * mm});
            skPoint(sketch, "E10.8.0.0", {"position": v(29.68, -29) * mm});
            skLineSegment(sketch, "E10.8.0.1", {"start": v(29.68, -27.5) * mm, "end": v(32.28, -26) * mm});
            skLineSegment(sketch, "E10.8.0.2", {"start": v(32.28, -26) * mm, "end": v(34.87, -27.5) * mm});
            skLineSegment(sketch, "E10.8.0.3", {"start": v(29.68, -9.5) * mm, "end": v(32.28, -8) * mm});
            skLineSegment(sketch, "E10.8.0.4", {"start": v(34.87, -27.5) * mm, "end": v(34.87, -30.5) * mm});
            skLineSegment(sketch, "E10.8.0.5", {"start": v(34.87, -30.5) * mm, "end": v(32.28, -32) * mm});
            skLineSegment(sketch, "E10.8.0.6", {"start": v(32.28, -8) * mm, "end": v(34.87, -9.5) * mm});
            skLineSegment(sketch, "E10.8.0.7", {"start": v(32.28, -32) * mm, "end": v(29.68, -30.5) * mm});
            skLineSegment(sketch, "E10.8.0.8", {"start": v(34.87, -9.5) * mm, "end": v(34.87, -12.5) * mm});
            skLineSegment(sketch, "E10.8.0.9", {"start": v(32.63, 12) * mm, "end": v(30.03, 13.5) * mm});
            skPoint(sketch, "E10.8.0.10", {"position": v(30.03, 24) * mm});
            skLineSegment(sketch, "E10.8.0.11", {"start": v(30.03, 16.5) * mm, "end": v(32.63, 18) * mm});
            skLineSegment(sketch, "E10.8.0.12", {"start": v(32.63, 18) * mm, "end": v(35.22, 16.5) * mm});
            skLineSegment(sketch, "E10.8.0.13", {"start": v(35.22, 16.5) * mm, "end": v(35.22, 13.5) * mm});
            skLineSegment(sketch, "E10.8.0.14", {"start": v(35.22, 13.5) * mm, "end": v(32.63, 12) * mm});
            skLineSegment(sketch, "E10.8.0.15", {"start": v(30.03, 25.5) * mm, "end": v(32.63, 27) * mm});
            skLineSegment(sketch, "E10.8.0.16", {"start": v(32.63, 27) * mm, "end": v(35.22, 25.5) * mm});
            skLineSegment(sketch, "E10.8.0.17", {"start": v(35.22, 25.5) * mm, "end": v(35.22, 22.5) * mm});
            skLineSegment(sketch, "E10.8.0.18", {"start": v(35.22, 22.5) * mm, "end": v(32.63, 21) * mm});
            skLineSegment(sketch, "E10.8.0.19", {"start": v(34.87, -12.5) * mm, "end": v(32.28, -14) * mm});
            skLineSegment(sketch, "E10.8.0.20", {"start": v(32.63, 21) * mm, "end": v(30.03, 22.5) * mm});
            skLineSegment(sketch, "E10.8.0.21", {"start": v(32.28, -14) * mm, "end": v(29.68, -12.5) * mm});
            skPoint(sketch, "E10.8.0.22", {"position": v(30.03, 15) * mm});
            skPoint(sketch, "E10.8.0.23", {"position": v(30.03, 6) * mm});
            skLineSegment(sketch, "E10.8.0.24", {"start": v(32.28, -17) * mm, "end": v(34.87, -18.5) * mm});
            skPoint(sketch, "E10.8.0.25", {"position": v(29.68, -11) * mm});
            skLineSegment(sketch, "E10.8.0.26", {"start": v(29.68, -18.5) * mm, "end": v(32.28, -17) * mm});
            skLineSegment(sketch, "E10.8.0.27", {"start": v(30.03, 7.5) * mm, "end": v(32.63, 9) * mm});
            skLineSegment(sketch, "E10.8.0.28", {"start": v(34.87, -18.5) * mm, "end": v(34.87, -21.5) * mm});
            skLineSegment(sketch, "E10.8.0.29", {"start": v(32.28, -23) * mm, "end": v(29.68, -21.5) * mm});
            skLineSegment(sketch, "E10.8.0.30", {"start": v(35.22, 7.5) * mm, "end": v(35.22, 4.5) * mm});
            skPoint(sketch, "E10.8.0.31", {"position": v(29.68, -20) * mm});
            skLineSegment(sketch, "E10.8.0.32", {"start": v(32.63, 9) * mm, "end": v(35.22, 7.5) * mm});
            skLineSegment(sketch, "E10.8.0.33", {"start": v(34.87, -21.5) * mm, "end": v(32.28, -23) * mm});
            skLineSegment(sketch, "E10.8.0.34", {"start": v(32.63, 3) * mm, "end": v(30.03, 4.5) * mm});
            skLineSegment(sketch, "E10.8.0.35", {"start": v(35.22, 4.5) * mm, "end": v(32.63, 3) * mm});
            skCircle(sketch, "E10.8.0.36", {"center": v(32.28, -29) * mm, "radius": 2.6 * mm, "construction": true});
            skCircle(sketch, "E10.8.0.37", {"center": v(32.28, -11) * mm, "radius": 2.6 * mm, "construction": true});
            skLineSegment(sketch, "E10.8.0.38", {"start": v(29.68, -12.5) * mm, "end": v(29.68, -9.5) * mm});
            skLineSegment(sketch, "E10.8.0.39", {"start": v(30.03, 4.5) * mm, "end": v(30.03, 7.5) * mm});
            skCircle(sketch, "E10.8.0.40", {"center": v(32.63, 6) * mm, "radius": 2.6 * mm, "construction": true});
            skCircle(sketch, "E10.8.0.41", {"center": v(32.63, 15) * mm, "radius": 2.6 * mm, "construction": true});
            skLineSegment(sketch, "E10.8.0.42", {"start": v(30.03, 13.5) * mm, "end": v(30.03, 16.5) * mm});
            skCircle(sketch, "E10.8.0.43", {"center": v(32.63, 24) * mm, "radius": 2.6 * mm, "construction": true});
            skLineSegment(sketch, "E10.8.0.44", {"start": v(30.03, 22.5) * mm, "end": v(30.03, 25.5) * mm});
            skCircle(sketch, "E10.8.0.45", {"center": v(32.28, -20) * mm, "radius": 2.6 * mm, "construction": true});
            skLineSegment(sketch, "E10.8.0.46", {"start": v(29.68, -21.5) * mm, "end": v(29.68, -18.5) * mm});
            skLineSegment(sketch, "E10.8.0.47", {"start": v(29.68, -30.5) * mm, "end": v(29.68, -27.5) * mm});
            skPoint(sketch, "E10.9.0.0", {"position": v(39.68, -29) * mm});
            skLineSegment(sketch, "E10.9.0.1", {"start": v(39.68, -27.5) * mm, "end": v(42.28, -26) * mm});
            skLineSegment(sketch, "E10.9.0.2", {"start": v(42.28, -26) * mm, "end": v(44.87, -27.5) * mm});
            skLineSegment(sketch, "E10.9.0.3", {"start": v(39.68, -9.5) * mm, "end": v(42.28, -8) * mm});
            skLineSegment(sketch, "E10.9.0.4", {"start": v(44.87, -27.5) * mm, "end": v(44.87, -30.5) * mm});
            skLineSegment(sketch, "E10.9.0.5", {"start": v(44.87, -30.5) * mm, "end": v(42.28, -32) * mm});
            skLineSegment(sketch, "E10.9.0.6", {"start": v(42.28, -8) * mm, "end": v(44.87, -9.5) * mm});
            skLineSegment(sketch, "E10.9.0.7", {"start": v(42.28, -32) * mm, "end": v(39.68, -30.5) * mm});
            skLineSegment(sketch, "E10.9.0.8", {"start": v(44.87, -9.5) * mm, "end": v(44.87, -12.5) * mm});
            skLineSegment(sketch, "E10.9.0.9", {"start": v(42.63, 12) * mm, "end": v(40.03, 13.5) * mm});
            skPoint(sketch, "E10.9.0.10", {"position": v(40.03, 24) * mm});
            skLineSegment(sketch, "E10.9.0.11", {"start": v(40.03, 16.5) * mm, "end": v(42.63, 18) * mm});
            skLineSegment(sketch, "E10.9.0.12", {"start": v(42.63, 18) * mm, "end": v(45.22, 16.5) * mm});
            skLineSegment(sketch, "E10.9.0.13", {"start": v(45.22, 16.5) * mm, "end": v(45.22, 13.5) * mm});
            skLineSegment(sketch, "E10.9.0.14", {"start": v(45.22, 13.5) * mm, "end": v(42.63, 12) * mm});
            skLineSegment(sketch, "E10.9.0.15", {"start": v(40.03, 25.5) * mm, "end": v(42.63, 27) * mm});
            skLineSegment(sketch, "E10.9.0.16", {"start": v(42.63, 27) * mm, "end": v(45.22, 25.5) * mm});
            skLineSegment(sketch, "E10.9.0.17", {"start": v(45.22, 25.5) * mm, "end": v(45.22, 22.5) * mm});
            skLineSegment(sketch, "E10.9.0.18", {"start": v(45.22, 22.5) * mm, "end": v(42.63, 21) * mm});
            skLineSegment(sketch, "E10.9.0.19", {"start": v(44.87, -12.5) * mm, "end": v(42.28, -14) * mm});
            skLineSegment(sketch, "E10.9.0.20", {"start": v(42.63, 21) * mm, "end": v(40.03, 22.5) * mm});
            skLineSegment(sketch, "E10.9.0.21", {"start": v(42.28, -14) * mm, "end": v(39.68, -12.5) * mm});
            skPoint(sketch, "E10.9.0.22", {"position": v(40.03, 15) * mm});
            skPoint(sketch, "E10.9.0.23", {"position": v(40.03, 6) * mm});
            skLineSegment(sketch, "E10.9.0.24", {"start": v(42.28, -17) * mm, "end": v(44.87, -18.5) * mm});
            skPoint(sketch, "E10.9.0.25", {"position": v(39.68, -11) * mm});
            skLineSegment(sketch, "E10.9.0.26", {"start": v(39.68, -18.5) * mm, "end": v(42.28, -17) * mm});
            skLineSegment(sketch, "E10.9.0.27", {"start": v(40.03, 7.5) * mm, "end": v(42.63, 9) * mm});
            skLineSegment(sketch, "E10.9.0.28", {"start": v(44.87, -18.5) * mm, "end": v(44.87, -21.5) * mm});
            skLineSegment(sketch, "E10.9.0.29", {"start": v(42.28, -23) * mm, "end": v(39.68, -21.5) * mm});
            skLineSegment(sketch, "E10.9.0.30", {"start": v(45.22, 7.5) * mm, "end": v(45.22, 4.5) * mm});
            skPoint(sketch, "E10.9.0.31", {"position": v(39.68, -20) * mm});
            skLineSegment(sketch, "E10.9.0.32", {"start": v(42.63, 9) * mm, "end": v(45.22, 7.5) * mm});
            skLineSegment(sketch, "E10.9.0.33", {"start": v(44.87, -21.5) * mm, "end": v(42.28, -23) * mm});
            skLineSegment(sketch, "E10.9.0.34", {"start": v(42.63, 3) * mm, "end": v(40.03, 4.5) * mm});
            skLineSegment(sketch, "E10.9.0.35", {"start": v(45.22, 4.5) * mm, "end": v(42.63, 3) * mm});
            skCircle(sketch, "E10.9.0.36", {"center": v(42.28, -29) * mm, "radius": 2.6 * mm, "construction": true});
            skCircle(sketch, "E10.9.0.37", {"center": v(42.28, -11) * mm, "radius": 2.6 * mm, "construction": true});
            skLineSegment(sketch, "E10.9.0.38", {"start": v(39.68, -12.5) * mm, "end": v(39.68, -9.5) * mm});
            skLineSegment(sketch, "E10.9.0.39", {"start": v(40.03, 4.5) * mm, "end": v(40.03, 7.5) * mm});
            skCircle(sketch, "E10.9.0.40", {"center": v(42.63, 6) * mm, "radius": 2.6 * mm, "construction": true});
            skCircle(sketch, "E10.9.0.41", {"center": v(42.63, 15) * mm, "radius": 2.6 * mm, "construction": true});
            skLineSegment(sketch, "E10.9.0.42", {"start": v(40.03, 13.5) * mm, "end": v(40.03, 16.5) * mm});
            skCircle(sketch, "E10.9.0.43", {"center": v(42.63, 24) * mm, "radius": 2.6 * mm, "construction": true});
            skLineSegment(sketch, "E10.9.0.44", {"start": v(40.03, 22.5) * mm, "end": v(40.03, 25.5) * mm});
            skCircle(sketch, "E10.9.0.45", {"center": v(42.28, -20) * mm, "radius": 2.6 * mm, "construction": true});
            skLineSegment(sketch, "E10.9.0.46", {"start": v(39.68, -21.5) * mm, "end": v(39.68, -18.5) * mm});
            skLineSegment(sketch, "E10.9.0.47", {"start": v(39.68, -30.5) * mm, "end": v(39.68, -27.5) * mm});
            skPoint(sketch, "E10.10.0.0", {"position": v(49.68, -29) * mm});
            skLineSegment(sketch, "E10.10.0.1", {"start": v(49.68, -27.5) * mm, "end": v(52.28, -26) * mm});
            skLineSegment(sketch, "E10.10.0.2", {"start": v(52.28, -26) * mm, "end": v(54.87, -27.5) * mm});
            skLineSegment(sketch, "E10.10.0.3", {"start": v(49.68, -9.5) * mm, "end": v(52.28, -8) * mm});
            skLineSegment(sketch, "E10.10.0.4", {"start": v(54.87, -27.5) * mm, "end": v(54.87, -30.5) * mm});
            skLineSegment(sketch, "E10.10.0.5", {"start": v(54.87, -30.5) * mm, "end": v(52.28, -32) * mm});
            skLineSegment(sketch, "E10.10.0.6", {"start": v(52.28, -8) * mm, "end": v(54.87, -9.5) * mm});
            skLineSegment(sketch, "E10.10.0.7", {"start": v(52.28, -32) * mm, "end": v(49.68, -30.5) * mm});
            skLineSegment(sketch, "E10.10.0.8", {"start": v(54.87, -9.5) * mm, "end": v(54.87, -12.5) * mm});
            skLineSegment(sketch, "E10.10.0.9", {"start": v(52.63, 12) * mm, "end": v(50.03, 13.5) * mm});
            skPoint(sketch, "E10.10.0.10", {"position": v(50.03, 24) * mm});
            skLineSegment(sketch, "E10.10.0.11", {"start": v(50.03, 16.5) * mm, "end": v(52.63, 18) * mm});
            skLineSegment(sketch, "E10.10.0.12", {"start": v(52.63, 18) * mm, "end": v(55.22, 16.5) * mm});
            skLineSegment(sketch, "E10.10.0.13", {"start": v(55.22, 16.5) * mm, "end": v(55.22, 13.5) * mm});
            skLineSegment(sketch, "E10.10.0.14", {"start": v(55.22, 13.5) * mm, "end": v(52.63, 12) * mm});
            skLineSegment(sketch, "E10.10.0.15", {"start": v(50.03, 25.5) * mm, "end": v(52.63, 27) * mm});
            skLineSegment(sketch, "E10.10.0.16", {"start": v(52.63, 27) * mm, "end": v(55.22, 25.5) * mm});
            skLineSegment(sketch, "E10.10.0.17", {"start": v(55.22, 25.5) * mm, "end": v(55.22, 22.5) * mm});
            skLineSegment(sketch, "E10.10.0.18", {"start": v(55.22, 22.5) * mm, "end": v(52.63, 21) * mm});
            skLineSegment(sketch, "E10.10.0.19", {"start": v(54.87, -12.5) * mm, "end": v(52.28, -14) * mm});
            skLineSegment(sketch, "E10.10.0.20", {"start": v(52.63, 21) * mm, "end": v(50.03, 22.5) * mm});
            skLineSegment(sketch, "E10.10.0.21", {"start": v(52.28, -14) * mm, "end": v(49.68, -12.5) * mm});
            skPoint(sketch, "E10.10.0.22", {"position": v(50.03, 15) * mm});
            skPoint(sketch, "E10.10.0.23", {"position": v(50.03, 6) * mm});
            skLineSegment(sketch, "E10.10.0.24", {"start": v(52.28, -17) * mm, "end": v(54.87, -18.5) * mm});
            skPoint(sketch, "E10.10.0.25", {"position": v(49.68, -11) * mm});
            skLineSegment(sketch, "E10.10.0.26", {"start": v(49.68, -18.5) * mm, "end": v(52.28, -17) * mm});
            skLineSegment(sketch, "E10.10.0.27", {"start": v(50.03, 7.5) * mm, "end": v(52.63, 9) * mm});
            skLineSegment(sketch, "E10.10.0.28", {"start": v(54.87, -18.5) * mm, "end": v(54.87, -21.5) * mm});
            skLineSegment(sketch, "E10.10.0.29", {"start": v(52.28, -23) * mm, "end": v(49.68, -21.5) * mm});
            skLineSegment(sketch, "E10.10.0.30", {"start": v(55.22, 7.5) * mm, "end": v(55.22, 4.5) * mm});
            skPoint(sketch, "E10.10.0.31", {"position": v(49.68, -20) * mm});
            skLineSegment(sketch, "E10.10.0.32", {"start": v(52.63, 9) * mm, "end": v(55.22, 7.5) * mm});
            skLineSegment(sketch, "E10.10.0.33", {"start": v(54.87, -21.5) * mm, "end": v(52.28, -23) * mm});
            skLineSegment(sketch, "E10.10.0.34", {"start": v(52.63, 3) * mm, "end": v(50.03, 4.5) * mm});
            skLineSegment(sketch, "E10.10.0.35", {"start": v(55.22, 4.5) * mm, "end": v(52.63, 3) * mm});
            skCircle(sketch, "E10.10.0.36", {"center": v(52.28, -29) * mm, "radius": 2.6 * mm, "construction": true});
            skCircle(sketch, "E10.10.0.37", {"center": v(52.28, -11) * mm, "radius": 2.6 * mm, "construction": true});
            skLineSegment(sketch, "E10.10.0.38", {"start": v(49.68, -12.5) * mm, "end": v(49.68, -9.5) * mm});
            skLineSegment(sketch, "E10.10.0.39", {"start": v(50.03, 4.5) * mm, "end": v(50.03, 7.5) * mm});
            skCircle(sketch, "E10.10.0.40", {"center": v(52.63, 6) * mm, "radius": 2.6 * mm, "construction": true});
            skCircle(sketch, "E10.10.0.41", {"center": v(52.63, 15) * mm, "radius": 2.6 * mm, "construction": true});
            skLineSegment(sketch, "E10.10.0.42", {"start": v(50.03, 13.5) * mm, "end": v(50.03, 16.5) * mm});
            skCircle(sketch, "E10.10.0.43", {"center": v(52.63, 24) * mm, "radius": 2.6 * mm, "construction": true});
            skLineSegment(sketch, "E10.10.0.44", {"start": v(50.03, 22.5) * mm, "end": v(50.03, 25.5) * mm});
            skCircle(sketch, "E10.10.0.45", {"center": v(52.28, -20) * mm, "radius": 2.6 * mm, "construction": true});
            skLineSegment(sketch, "E10.10.0.46", {"start": v(49.68, -21.5) * mm, "end": v(49.68, -18.5) * mm});
            skLineSegment(sketch, "E10.10.0.47", {"start": v(49.68, -30.5) * mm, "end": v(49.68, -27.5) * mm});
            skPoint(sketch, "E10.11.0.0", {"position": v(59.68, -29) * mm});
            skLineSegment(sketch, "E10.11.0.1", {"start": v(59.68, -27.5) * mm, "end": v(62.28, -26) * mm});
            skLineSegment(sketch, "E10.11.0.2", {"start": v(62.28, -26) * mm, "end": v(64.87, -27.5) * mm});
            skLineSegment(sketch, "E10.11.0.3", {"start": v(59.68, -9.5) * mm, "end": v(62.28, -8) * mm});
            skLineSegment(sketch, "E10.11.0.4", {"start": v(64.87, -27.5) * mm, "end": v(64.87, -30.5) * mm});
            skLineSegment(sketch, "E10.11.0.5", {"start": v(64.87, -30.5) * mm, "end": v(62.28, -32) * mm});
            skLineSegment(sketch, "E10.11.0.6", {"start": v(62.28, -8) * mm, "end": v(64.87, -9.5) * mm});
            skLineSegment(sketch, "E10.11.0.7", {"start": v(62.28, -32) * mm, "end": v(59.68, -30.5) * mm});
            skLineSegment(sketch, "E10.11.0.8", {"start": v(64.87, -9.5) * mm, "end": v(64.87, -12.5) * mm});
            skLineSegment(sketch, "E10.11.0.9", {"start": v(62.63, 12) * mm, "end": v(60.03, 13.5) * mm});
            skPoint(sketch, "E10.11.0.10", {"position": v(60.03, 24) * mm});
            skLineSegment(sketch, "E10.11.0.11", {"start": v(60.03, 16.5) * mm, "end": v(62.63, 18) * mm});
            skLineSegment(sketch, "E10.11.0.12", {"start": v(62.63, 18) * mm, "end": v(65.22, 16.5) * mm});
            skLineSegment(sketch, "E10.11.0.13", {"start": v(65.22, 16.5) * mm, "end": v(65.22, 13.5) * mm});
            skLineSegment(sketch, "E10.11.0.14", {"start": v(65.22, 13.5) * mm, "end": v(62.63, 12) * mm});
            skLineSegment(sketch, "E10.11.0.15", {"start": v(60.03, 25.5) * mm, "end": v(62.63, 27) * mm});
            skLineSegment(sketch, "E10.11.0.16", {"start": v(62.63, 27) * mm, "end": v(65.22, 25.5) * mm});
            skLineSegment(sketch, "E10.11.0.17", {"start": v(65.22, 25.5) * mm, "end": v(65.22, 22.5) * mm});
            skLineSegment(sketch, "E10.11.0.18", {"start": v(65.22, 22.5) * mm, "end": v(62.63, 21) * mm});
            skLineSegment(sketch, "E10.11.0.19", {"start": v(64.87, -12.5) * mm, "end": v(62.28, -14) * mm});
            skLineSegment(sketch, "E10.11.0.20", {"start": v(62.63, 21) * mm, "end": v(60.03, 22.5) * mm});
            skLineSegment(sketch, "E10.11.0.21", {"start": v(62.28, -14) * mm, "end": v(59.68, -12.5) * mm});
            skPoint(sketch, "E10.11.0.22", {"position": v(60.03, 15) * mm});
            skPoint(sketch, "E10.11.0.23", {"position": v(60.03, 6) * mm});
            skLineSegment(sketch, "E10.11.0.24", {"start": v(62.28, -17) * mm, "end": v(64.87, -18.5) * mm});
            skPoint(sketch, "E10.11.0.25", {"position": v(59.68, -11) * mm});
            skLineSegment(sketch, "E10.11.0.26", {"start": v(59.68, -18.5) * mm, "end": v(62.28, -17) * mm});
            skLineSegment(sketch, "E10.11.0.27", {"start": v(60.03, 7.5) * mm, "end": v(62.63, 9) * mm});
            skLineSegment(sketch, "E10.11.0.28", {"start": v(64.87, -18.5) * mm, "end": v(64.87, -21.5) * mm});
            skLineSegment(sketch, "E10.11.0.29", {"start": v(62.28, -23) * mm, "end": v(59.68, -21.5) * mm});
            skLineSegment(sketch, "E10.11.0.30", {"start": v(65.22, 7.5) * mm, "end": v(65.22, 4.5) * mm});
            skPoint(sketch, "E10.11.0.31", {"position": v(59.68, -20) * mm});
            skLineSegment(sketch, "E10.11.0.32", {"start": v(62.63, 9) * mm, "end": v(65.22, 7.5) * mm});
            skLineSegment(sketch, "E10.11.0.33", {"start": v(64.87, -21.5) * mm, "end": v(62.28, -23) * mm});
            skLineSegment(sketch, "E10.11.0.34", {"start": v(62.63, 3) * mm, "end": v(60.03, 4.5) * mm});
            skLineSegment(sketch, "E10.11.0.35", {"start": v(65.22, 4.5) * mm, "end": v(62.63, 3) * mm});
            skCircle(sketch, "E10.11.0.36", {"center": v(62.28, -29) * mm, "radius": 2.6 * mm, "construction": true});
            skCircle(sketch, "E10.11.0.37", {"center": v(62.28, -11) * mm, "radius": 2.6 * mm, "construction": true});
            skLineSegment(sketch, "E10.11.0.38", {"start": v(59.68, -12.5) * mm, "end": v(59.68, -9.5) * mm});
            skLineSegment(sketch, "E10.11.0.39", {"start": v(60.03, 4.5) * mm, "end": v(60.03, 7.5) * mm});
            skCircle(sketch, "E10.11.0.40", {"center": v(62.63, 6) * mm, "radius": 2.6 * mm, "construction": true});
            skCircle(sketch, "E10.11.0.41", {"center": v(62.63, 15) * mm, "radius": 2.6 * mm, "construction": true});
            skLineSegment(sketch, "E10.11.0.42", {"start": v(60.03, 13.5) * mm, "end": v(60.03, 16.5) * mm});
            skCircle(sketch, "E10.11.0.43", {"center": v(62.63, 24) * mm, "radius": 2.6 * mm, "construction": true});
            skLineSegment(sketch, "E10.11.0.44", {"start": v(60.03, 22.5) * mm, "end": v(60.03, 25.5) * mm});
            skCircle(sketch, "E10.11.0.45", {"center": v(62.28, -20) * mm, "radius": 2.6 * mm, "construction": true});
            skLineSegment(sketch, "E10.11.0.46", {"start": v(59.68, -21.5) * mm, "end": v(59.68, -18.5) * mm});
            skLineSegment(sketch, "E10.11.0.47", {"start": v(59.68, -30.5) * mm, "end": v(59.68, -27.5) * mm});
            skSolve(sketch);
        }
        {
            var Q0;
            Q0 = qSketchRegion(id + "F3", true);
            extrude(context, id + "F4", {"entities" : qUnion([Q0]), "operationType" : NewBodyOperationType.REMOVE, "oppositeDirection" : true, "depth" : 5 * mm});
        }
        {
            var Q0;
            Q0=qCreatedBy(makeId("Front.planeOp"),FACE);
            var sketch = newSketch(context, id + "F5", { "sketchPlane" : qUnion([Q0])});
            skCircle(sketch, "E11.cCircle", {"center": v(-46.44, 44.4) * mm, "radius": 2.6 * mm, "construction": true});
            skLineSegment(sketch, "E11.0", {"start": v(-47.94, 47) * mm, "end": v(-44.94, 47) * mm});
            skLineSegment(sketch, "E11.1", {"start": v(-44.94, 47) * mm, "end": v(-43.44, 44.4) * mm});
            skLineSegment(sketch, "E11.2", {"start": v(-43.44, 44.4) * mm, "end": v(-44.94, 41.8) * mm});
            skLineSegment(sketch, "E11.3", {"start": v(-44.94, 41.8) * mm, "end": v(-47.94, 41.8) * mm});
            skLineSegment(sketch, "E11.4", {"start": v(-47.94, 41.8) * mm, "end": v(-49.44, 44.4) * mm});
            skLineSegment(sketch, "E11.5", {"start": v(-49.44, 44.4) * mm, "end": v(-47.94, 47) * mm});
            skPoint(sketch, "E11.0.midPoint", {"position": v(-46.44, 47) * mm});
            skLineSegment(sketch, "E12.0.1.0", {"start": v(-49.44, 36.4) * mm, "end": v(-47.94, 39) * mm});
            skLineSegment(sketch, "E12.0.1.1", {"start": v(-47.94, 33.8) * mm, "end": v(-49.44, 36.4) * mm});
            skLineSegment(sketch, "E12.0.1.2", {"start": v(-44.94, 39) * mm, "end": v(-43.44, 36.4) * mm});
            skLineSegment(sketch, "E12.0.1.3", {"start": v(-47.94, 39) * mm, "end": v(-44.94, 39) * mm});
            skLineSegment(sketch, "E12.0.1.4", {"start": v(-44.94, 33.8) * mm, "end": v(-47.94, 33.8) * mm});
            skLineSegment(sketch, "E12.0.1.5", {"start": v(-43.44, 36.4) * mm, "end": v(-44.94, 33.8) * mm});
            skCircle(sketch, "E12.0.1.6", {"center": v(-46.44, 36.4) * mm, "radius": 2.6 * mm, "construction": true});
            skPoint(sketch, "E12.0.1.7", {"position": v(-46.44, 39) * mm});
            skLineSegment(sketch, "E12.0.2.0", {"start": v(-49.44, 28.4) * mm, "end": v(-47.94, 31) * mm});
            skLineSegment(sketch, "E12.0.2.1", {"start": v(-47.94, 25.8) * mm, "end": v(-49.44, 28.4) * mm});
            skLineSegment(sketch, "E12.0.2.2", {"start": v(-44.94, 31) * mm, "end": v(-43.44, 28.4) * mm});
            skLineSegment(sketch, "E12.0.2.3", {"start": v(-47.94, 31) * mm, "end": v(-44.94, 31) * mm});
            skLineSegment(sketch, "E12.0.2.4", {"start": v(-44.94, 25.8) * mm, "end": v(-47.94, 25.8) * mm});
            skLineSegment(sketch, "E12.0.2.5", {"start": v(-43.44, 28.4) * mm, "end": v(-44.94, 25.8) * mm});
            skCircle(sketch, "E12.0.2.6", {"center": v(-46.44, 28.4) * mm, "radius": 2.6 * mm, "construction": true});
            skPoint(sketch, "E12.0.2.7", {"position": v(-46.44, 31) * mm});
            skLineSegment(sketch, "E12.0.3.0", {"start": v(-49.44, 20.4) * mm, "end": v(-47.94, 23) * mm});
            skLineSegment(sketch, "E12.0.3.1", {"start": v(-47.94, 17.8) * mm, "end": v(-49.44, 20.4) * mm});
            skLineSegment(sketch, "E12.0.3.2", {"start": v(-44.94, 23) * mm, "end": v(-43.44, 20.4) * mm});
            skLineSegment(sketch, "E12.0.3.3", {"start": v(-47.94, 23) * mm, "end": v(-44.94, 23) * mm});
            skLineSegment(sketch, "E12.0.3.4", {"start": v(-44.94, 17.8) * mm, "end": v(-47.94, 17.8) * mm});
            skLineSegment(sketch, "E12.0.3.5", {"start": v(-43.44, 20.4) * mm, "end": v(-44.94, 17.8) * mm});
            skCircle(sketch, "E12.0.3.6", {"center": v(-46.44, 20.4) * mm, "radius": 2.6 * mm, "construction": true});
            skPoint(sketch, "E12.0.3.7", {"position": v(-46.44, 23) * mm});
            skLineSegment(sketch, "E12.0.4.0", {"start": v(-49.44, 12.4) * mm, "end": v(-47.94, 15) * mm});
            skLineSegment(sketch, "E12.0.4.1", {"start": v(-47.94, 9.8) * mm, "end": v(-49.44, 12.4) * mm});
            skLineSegment(sketch, "E12.0.4.2", {"start": v(-44.94, 15) * mm, "end": v(-43.44, 12.4) * mm});
            skLineSegment(sketch, "E12.0.4.3", {"start": v(-47.94, 15) * mm, "end": v(-44.94, 15) * mm});
            skLineSegment(sketch, "E12.0.4.4", {"start": v(-44.94, 9.8) * mm, "end": v(-47.94, 9.8) * mm});
            skLineSegment(sketch, "E12.0.4.5", {"start": v(-43.44, 12.4) * mm, "end": v(-44.94, 9.8) * mm});
            skCircle(sketch, "E12.0.4.6", {"center": v(-46.44, 12.4) * mm, "radius": 2.6 * mm, "construction": true});
            skPoint(sketch, "E12.0.4.7", {"position": v(-46.44, 15) * mm});
            skLineSegment(sketch, "E12.1.0.0", {"start": v(-40.44, 44.4) * mm, "end": v(-38.94, 47) * mm});
            skLineSegment(sketch, "E12.1.0.1", {"start": v(-38.94, 41.8) * mm, "end": v(-40.44, 44.4) * mm});
            skLineSegment(sketch, "E12.1.0.2", {"start": v(-35.94, 47) * mm, "end": v(-34.44, 44.4) * mm});
            skLineSegment(sketch, "E12.1.0.3", {"start": v(-38.94, 47) * mm, "end": v(-35.94, 47) * mm});
            skLineSegment(sketch, "E12.1.0.4", {"start": v(-35.94, 41.8) * mm, "end": v(-38.94, 41.8) * mm});
            skLineSegment(sketch, "E12.1.0.5", {"start": v(-34.44, 44.4) * mm, "end": v(-35.94, 41.8) * mm});
            skCircle(sketch, "E12.1.0.6", {"center": v(-37.44, 44.4) * mm, "radius": 2.6 * mm, "construction": true});
            skPoint(sketch, "E12.1.0.7", {"position": v(-37.44, 47) * mm});
            skLineSegment(sketch, "E12.1.1.0", {"start": v(-40.44, 36.4) * mm, "end": v(-38.94, 39) * mm});
            skLineSegment(sketch, "E12.1.1.1", {"start": v(-38.94, 33.8) * mm, "end": v(-40.44, 36.4) * mm});
            skLineSegment(sketch, "E12.1.1.2", {"start": v(-35.94, 39) * mm, "end": v(-34.44, 36.4) * mm});
            skLineSegment(sketch, "E12.1.1.3", {"start": v(-38.94, 39) * mm, "end": v(-35.94, 39) * mm});
            skLineSegment(sketch, "E12.1.1.4", {"start": v(-35.94, 33.8) * mm, "end": v(-38.94, 33.8) * mm});
            skLineSegment(sketch, "E12.1.1.5", {"start": v(-34.44, 36.4) * mm, "end": v(-35.94, 33.8) * mm});
            skCircle(sketch, "E12.1.1.6", {"center": v(-37.44, 36.4) * mm, "radius": 2.6 * mm, "construction": true});
            skPoint(sketch, "E12.1.1.7", {"position": v(-37.44, 39) * mm});
            skLineSegment(sketch, "E12.1.2.0", {"start": v(-40.44, 28.4) * mm, "end": v(-38.94, 31) * mm});
            skLineSegment(sketch, "E12.1.2.1", {"start": v(-38.94, 25.8) * mm, "end": v(-40.44, 28.4) * mm});
            skLineSegment(sketch, "E12.1.2.2", {"start": v(-35.94, 31) * mm, "end": v(-34.44, 28.4) * mm});
            skLineSegment(sketch, "E12.1.2.3", {"start": v(-38.94, 31) * mm, "end": v(-35.94, 31) * mm});
            skLineSegment(sketch, "E12.1.2.4", {"start": v(-35.94, 25.8) * mm, "end": v(-38.94, 25.8) * mm});
            skLineSegment(sketch, "E12.1.2.5", {"start": v(-34.44, 28.4) * mm, "end": v(-35.94, 25.8) * mm});
            skCircle(sketch, "E12.1.2.6", {"center": v(-37.44, 28.4) * mm, "radius": 2.6 * mm, "construction": true});
            skPoint(sketch, "E12.1.2.7", {"position": v(-37.44, 31) * mm});
            skLineSegment(sketch, "E12.1.3.0", {"start": v(-40.44, 20.4) * mm, "end": v(-38.94, 23) * mm});
            skLineSegment(sketch, "E12.1.3.1", {"start": v(-38.94, 17.8) * mm, "end": v(-40.44, 20.4) * mm});
            skLineSegment(sketch, "E12.1.3.2", {"start": v(-35.94, 23) * mm, "end": v(-34.44, 20.4) * mm});
            skLineSegment(sketch, "E12.1.3.3", {"start": v(-38.94, 23) * mm, "end": v(-35.94, 23) * mm});
            skLineSegment(sketch, "E12.1.3.4", {"start": v(-35.94, 17.8) * mm, "end": v(-38.94, 17.8) * mm});
            skLineSegment(sketch, "E12.1.3.5", {"start": v(-34.44, 20.4) * mm, "end": v(-35.94, 17.8) * mm});
            skCircle(sketch, "E12.1.3.6", {"center": v(-37.44, 20.4) * mm, "radius": 2.6 * mm, "construction": true});
            skPoint(sketch, "E12.1.3.7", {"position": v(-37.44, 23) * mm});
            skLineSegment(sketch, "E12.1.4.0", {"start": v(-40.44, 12.4) * mm, "end": v(-38.94, 15) * mm});
            skLineSegment(sketch, "E12.1.4.1", {"start": v(-38.94, 9.8) * mm, "end": v(-40.44, 12.4) * mm});
            skLineSegment(sketch, "E12.1.4.2", {"start": v(-35.94, 15) * mm, "end": v(-34.44, 12.4) * mm});
            skLineSegment(sketch, "E12.1.4.3", {"start": v(-38.94, 15) * mm, "end": v(-35.94, 15) * mm});
            skLineSegment(sketch, "E12.1.4.4", {"start": v(-35.94, 9.8) * mm, "end": v(-38.94, 9.8) * mm});
            skLineSegment(sketch, "E12.1.4.5", {"start": v(-34.44, 12.4) * mm, "end": v(-35.94, 9.8) * mm});
            skCircle(sketch, "E12.1.4.6", {"center": v(-37.44, 12.4) * mm, "radius": 2.6 * mm, "construction": true});
            skPoint(sketch, "E12.1.4.7", {"position": v(-37.44, 15) * mm});
            skLineSegment(sketch, "E12.2.0.0", {"start": v(-31.44, 44.4) * mm, "end": v(-29.94, 47) * mm});
            skLineSegment(sketch, "E12.2.0.1", {"start": v(-29.94, 41.8) * mm, "end": v(-31.44, 44.4) * mm});
            skLineSegment(sketch, "E12.2.0.2", {"start": v(-26.94, 47) * mm, "end": v(-25.44, 44.4) * mm});
            skLineSegment(sketch, "E12.2.0.3", {"start": v(-29.94, 47) * mm, "end": v(-26.94, 47) * mm});
            skLineSegment(sketch, "E12.2.0.4", {"start": v(-26.94, 41.8) * mm, "end": v(-29.94, 41.8) * mm});
            skLineSegment(sketch, "E12.2.0.5", {"start": v(-25.44, 44.4) * mm, "end": v(-26.94, 41.8) * mm});
            skCircle(sketch, "E12.2.0.6", {"center": v(-28.44, 44.4) * mm, "radius": 2.6 * mm, "construction": true});
            skPoint(sketch, "E12.2.0.7", {"position": v(-28.44, 47) * mm});
            skLineSegment(sketch, "E12.2.1.0", {"start": v(-31.44, 36.4) * mm, "end": v(-29.94, 39) * mm});
            skLineSegment(sketch, "E12.2.1.1", {"start": v(-29.94, 33.8) * mm, "end": v(-31.44, 36.4) * mm});
            skLineSegment(sketch, "E12.2.1.2", {"start": v(-26.94, 39) * mm, "end": v(-25.44, 36.4) * mm});
            skLineSegment(sketch, "E12.2.1.3", {"start": v(-29.94, 39) * mm, "end": v(-26.94, 39) * mm});
            skLineSegment(sketch, "E12.2.1.4", {"start": v(-26.94, 33.8) * mm, "end": v(-29.94, 33.8) * mm});
            skLineSegment(sketch, "E12.2.1.5", {"start": v(-25.44, 36.4) * mm, "end": v(-26.94, 33.8) * mm});
            skCircle(sketch, "E12.2.1.6", {"center": v(-28.44, 36.4) * mm, "radius": 2.6 * mm, "construction": true});
            skPoint(sketch, "E12.2.1.7", {"position": v(-28.44, 39) * mm});
            skLineSegment(sketch, "E12.2.2.0", {"start": v(-31.44, 28.4) * mm, "end": v(-29.94, 31) * mm});
            skLineSegment(sketch, "E12.2.2.1", {"start": v(-29.94, 25.8) * mm, "end": v(-31.44, 28.4) * mm});
            skLineSegment(sketch, "E12.2.2.2", {"start": v(-26.94, 31) * mm, "end": v(-25.44, 28.4) * mm});
            skLineSegment(sketch, "E12.2.2.3", {"start": v(-29.94, 31) * mm, "end": v(-26.94, 31) * mm});
            skLineSegment(sketch, "E12.2.2.4", {"start": v(-26.94, 25.8) * mm, "end": v(-29.94, 25.8) * mm});
            skLineSegment(sketch, "E12.2.2.5", {"start": v(-25.44, 28.4) * mm, "end": v(-26.94, 25.8) * mm});
            skCircle(sketch, "E12.2.2.6", {"center": v(-28.44, 28.4) * mm, "radius": 2.6 * mm, "construction": true});
            skPoint(sketch, "E12.2.2.7", {"position": v(-28.44, 31) * mm});
            skLineSegment(sketch, "E12.2.3.0", {"start": v(-31.44, 20.4) * mm, "end": v(-29.94, 23) * mm});
            skLineSegment(sketch, "E12.2.3.1", {"start": v(-29.94, 17.8) * mm, "end": v(-31.44, 20.4) * mm});
            skLineSegment(sketch, "E12.2.3.2", {"start": v(-26.94, 23) * mm, "end": v(-25.44, 20.4) * mm});
            skLineSegment(sketch, "E12.2.3.3", {"start": v(-29.94, 23) * mm, "end": v(-26.94, 23) * mm});
            skLineSegment(sketch, "E12.2.3.4", {"start": v(-26.94, 17.8) * mm, "end": v(-29.94, 17.8) * mm});
            skLineSegment(sketch, "E12.2.3.5", {"start": v(-25.44, 20.4) * mm, "end": v(-26.94, 17.8) * mm});
            skCircle(sketch, "E12.2.3.6", {"center": v(-28.44, 20.4) * mm, "radius": 2.6 * mm, "construction": true});
            skPoint(sketch, "E12.2.3.7", {"position": v(-28.44, 23) * mm});
            skLineSegment(sketch, "E12.2.4.0", {"start": v(-31.44, 12.4) * mm, "end": v(-29.94, 15) * mm});
            skLineSegment(sketch, "E12.2.4.1", {"start": v(-29.94, 9.8) * mm, "end": v(-31.44, 12.4) * mm});
            skLineSegment(sketch, "E12.2.4.2", {"start": v(-26.94, 15) * mm, "end": v(-25.44, 12.4) * mm});
            skLineSegment(sketch, "E12.2.4.3", {"start": v(-29.94, 15) * mm, "end": v(-26.94, 15) * mm});
            skLineSegment(sketch, "E12.2.4.4", {"start": v(-26.94, 9.8) * mm, "end": v(-29.94, 9.8) * mm});
            skLineSegment(sketch, "E12.2.4.5", {"start": v(-25.44, 12.4) * mm, "end": v(-26.94, 9.8) * mm});
            skCircle(sketch, "E12.2.4.6", {"center": v(-28.44, 12.4) * mm, "radius": 2.6 * mm, "construction": true});
            skPoint(sketch, "E12.2.4.7", {"position": v(-28.44, 15) * mm});
            skLineSegment(sketch, "E12.3.0.0", {"start": v(-22.44, 44.4) * mm, "end": v(-20.94, 47) * mm});
            skLineSegment(sketch, "E12.3.0.1", {"start": v(-20.94, 41.8) * mm, "end": v(-22.44, 44.4) * mm});
            skLineSegment(sketch, "E12.3.0.2", {"start": v(-17.94, 47) * mm, "end": v(-16.44, 44.4) * mm});
            skLineSegment(sketch, "E12.3.0.3", {"start": v(-20.94, 47) * mm, "end": v(-17.94, 47) * mm});
            skLineSegment(sketch, "E12.3.0.4", {"start": v(-17.94, 41.8) * mm, "end": v(-20.94, 41.8) * mm});
            skLineSegment(sketch, "E12.3.0.5", {"start": v(-16.44, 44.4) * mm, "end": v(-17.94, 41.8) * mm});
            skCircle(sketch, "E12.3.0.6", {"center": v(-19.44, 44.4) * mm, "radius": 2.6 * mm, "construction": true});
            skPoint(sketch, "E12.3.0.7", {"position": v(-19.44, 47) * mm});
            skLineSegment(sketch, "E12.3.1.0", {"start": v(-22.44, 36.4) * mm, "end": v(-20.94, 39) * mm});
            skLineSegment(sketch, "E12.3.1.1", {"start": v(-20.94, 33.8) * mm, "end": v(-22.44, 36.4) * mm});
            skLineSegment(sketch, "E12.3.1.2", {"start": v(-17.94, 39) * mm, "end": v(-16.44, 36.4) * mm});
            skLineSegment(sketch, "E12.3.1.3", {"start": v(-20.94, 39) * mm, "end": v(-17.94, 39) * mm});
            skLineSegment(sketch, "E12.3.1.4", {"start": v(-17.94, 33.8) * mm, "end": v(-20.94, 33.8) * mm});
            skLineSegment(sketch, "E12.3.1.5", {"start": v(-16.44, 36.4) * mm, "end": v(-17.94, 33.8) * mm});
            skCircle(sketch, "E12.3.1.6", {"center": v(-19.44, 36.4) * mm, "radius": 2.6 * mm, "construction": true});
            skPoint(sketch, "E12.3.1.7", {"position": v(-19.44, 39) * mm});
            skLineSegment(sketch, "E12.3.2.0", {"start": v(-22.44, 28.4) * mm, "end": v(-20.94, 31) * mm});
            skLineSegment(sketch, "E12.3.2.1", {"start": v(-20.94, 25.8) * mm, "end": v(-22.44, 28.4) * mm});
            skLineSegment(sketch, "E12.3.2.2", {"start": v(-17.94, 31) * mm, "end": v(-16.44, 28.4) * mm});
            skLineSegment(sketch, "E12.3.2.3", {"start": v(-20.94, 31) * mm, "end": v(-17.94, 31) * mm});
            skLineSegment(sketch, "E12.3.2.4", {"start": v(-17.94, 25.8) * mm, "end": v(-20.94, 25.8) * mm});
            skLineSegment(sketch, "E12.3.2.5", {"start": v(-16.44, 28.4) * mm, "end": v(-17.94, 25.8) * mm});
            skCircle(sketch, "E12.3.2.6", {"center": v(-19.44, 28.4) * mm, "radius": 2.6 * mm, "construction": true});
            skPoint(sketch, "E12.3.2.7", {"position": v(-19.44, 31) * mm});
            skLineSegment(sketch, "E12.3.3.0", {"start": v(-22.44, 20.4) * mm, "end": v(-20.94, 23) * mm});
            skLineSegment(sketch, "E12.3.3.1", {"start": v(-20.94, 17.8) * mm, "end": v(-22.44, 20.4) * mm});
            skLineSegment(sketch, "E12.3.3.2", {"start": v(-17.94, 23) * mm, "end": v(-16.44, 20.4) * mm});
            skLineSegment(sketch, "E12.3.3.3", {"start": v(-20.94, 23) * mm, "end": v(-17.94, 23) * mm});
            skLineSegment(sketch, "E12.3.3.4", {"start": v(-17.94, 17.8) * mm, "end": v(-20.94, 17.8) * mm});
            skLineSegment(sketch, "E12.3.3.5", {"start": v(-16.44, 20.4) * mm, "end": v(-17.94, 17.8) * mm});
            skCircle(sketch, "E12.3.3.6", {"center": v(-19.44, 20.4) * mm, "radius": 2.6 * mm, "construction": true});
            skPoint(sketch, "E12.3.3.7", {"position": v(-19.44, 23) * mm});
            skLineSegment(sketch, "E12.3.4.0", {"start": v(-22.44, 12.4) * mm, "end": v(-20.94, 15) * mm});
            skLineSegment(sketch, "E12.3.4.1", {"start": v(-20.94, 9.8) * mm, "end": v(-22.44, 12.4) * mm});
            skLineSegment(sketch, "E12.3.4.2", {"start": v(-17.94, 15) * mm, "end": v(-16.44, 12.4) * mm});
            skLineSegment(sketch, "E12.3.4.3", {"start": v(-20.94, 15) * mm, "end": v(-17.94, 15) * mm});
            skLineSegment(sketch, "E12.3.4.4", {"start": v(-17.94, 9.8) * mm, "end": v(-20.94, 9.8) * mm});
            skLineSegment(sketch, "E12.3.4.5", {"start": v(-16.44, 12.4) * mm, "end": v(-17.94, 9.8) * mm});
            skCircle(sketch, "E12.3.4.6", {"center": v(-19.44, 12.4) * mm, "radius": 2.6 * mm, "construction": true});
            skPoint(sketch, "E12.3.4.7", {"position": v(-19.44, 15) * mm});
            skLineSegment(sketch, "E12.4.0.0", {"start": v(-13.44, 44.4) * mm, "end": v(-11.94, 47) * mm});
            skLineSegment(sketch, "E12.4.0.1", {"start": v(-11.94, 41.8) * mm, "end": v(-13.44, 44.4) * mm});
            skLineSegment(sketch, "E12.4.0.2", {"start": v(-8.94, 47) * mm, "end": v(-7.44, 44.4) * mm});
            skLineSegment(sketch, "E12.4.0.3", {"start": v(-11.94, 47) * mm, "end": v(-8.94, 47) * mm});
            skLineSegment(sketch, "E12.4.0.4", {"start": v(-8.94, 41.8) * mm, "end": v(-11.94, 41.8) * mm});
            skLineSegment(sketch, "E12.4.0.5", {"start": v(-7.44, 44.4) * mm, "end": v(-8.94, 41.8) * mm});
            skCircle(sketch, "E12.4.0.6", {"center": v(-10.44, 44.4) * mm, "radius": 2.6 * mm, "construction": true});
            skPoint(sketch, "E12.4.0.7", {"position": v(-10.44, 47) * mm});
            skLineSegment(sketch, "E12.4.1.0", {"start": v(-13.44, 36.4) * mm, "end": v(-11.94, 39) * mm});
            skLineSegment(sketch, "E12.4.1.1", {"start": v(-11.94, 33.8) * mm, "end": v(-13.44, 36.4) * mm});
            skLineSegment(sketch, "E12.4.1.2", {"start": v(-8.94, 39) * mm, "end": v(-7.44, 36.4) * mm});
            skLineSegment(sketch, "E12.4.1.3", {"start": v(-11.94, 39) * mm, "end": v(-8.94, 39) * mm});
            skLineSegment(sketch, "E12.4.1.4", {"start": v(-8.94, 33.8) * mm, "end": v(-11.94, 33.8) * mm});
            skLineSegment(sketch, "E12.4.1.5", {"start": v(-7.44, 36.4) * mm, "end": v(-8.94, 33.8) * mm});
            skCircle(sketch, "E12.4.1.6", {"center": v(-10.44, 36.4) * mm, "radius": 2.6 * mm, "construction": true});
            skPoint(sketch, "E12.4.1.7", {"position": v(-10.44, 39) * mm});
            skLineSegment(sketch, "E12.4.2.0", {"start": v(-13.44, 28.4) * mm, "end": v(-11.94, 31) * mm});
            skLineSegment(sketch, "E12.4.2.1", {"start": v(-11.94, 25.8) * mm, "end": v(-13.44, 28.4) * mm});
            skLineSegment(sketch, "E12.4.2.2", {"start": v(-8.94, 31) * mm, "end": v(-7.44, 28.4) * mm});
            skLineSegment(sketch, "E12.4.2.3", {"start": v(-11.94, 31) * mm, "end": v(-8.94, 31) * mm});
            skLineSegment(sketch, "E12.4.2.4", {"start": v(-8.94, 25.8) * mm, "end": v(-11.94, 25.8) * mm});
            skLineSegment(sketch, "E12.4.2.5", {"start": v(-7.44, 28.4) * mm, "end": v(-8.94, 25.8) * mm});
            skCircle(sketch, "E12.4.2.6", {"center": v(-10.44, 28.4) * mm, "radius": 2.6 * mm, "construction": true});
            skPoint(sketch, "E12.4.2.7", {"position": v(-10.44, 31) * mm});
            skLineSegment(sketch, "E12.4.3.0", {"start": v(-13.44, 20.4) * mm, "end": v(-11.94, 23) * mm});
            skLineSegment(sketch, "E12.4.3.1", {"start": v(-11.94, 17.8) * mm, "end": v(-13.44, 20.4) * mm});
            skLineSegment(sketch, "E12.4.3.2", {"start": v(-8.94, 23) * mm, "end": v(-7.44, 20.4) * mm});
            skLineSegment(sketch, "E12.4.3.3", {"start": v(-11.94, 23) * mm, "end": v(-8.94, 23) * mm});
            skLineSegment(sketch, "E12.4.3.4", {"start": v(-8.94, 17.8) * mm, "end": v(-11.94, 17.8) * mm});
            skLineSegment(sketch, "E12.4.3.5", {"start": v(-7.44, 20.4) * mm, "end": v(-8.94, 17.8) * mm});
            skCircle(sketch, "E12.4.3.6", {"center": v(-10.44, 20.4) * mm, "radius": 2.6 * mm, "construction": true});
            skPoint(sketch, "E12.4.3.7", {"position": v(-10.44, 23) * mm});
            skLineSegment(sketch, "E12.4.4.0", {"start": v(-13.44, 12.4) * mm, "end": v(-11.94, 15) * mm});
            skLineSegment(sketch, "E12.4.4.1", {"start": v(-11.94, 9.8) * mm, "end": v(-13.44, 12.4) * mm});
            skLineSegment(sketch, "E12.4.4.2", {"start": v(-8.94, 15) * mm, "end": v(-7.44, 12.4) * mm});
            skLineSegment(sketch, "E12.4.4.3", {"start": v(-11.94, 15) * mm, "end": v(-8.94, 15) * mm});
            skLineSegment(sketch, "E12.4.4.4", {"start": v(-8.94, 9.8) * mm, "end": v(-11.94, 9.8) * mm});
            skLineSegment(sketch, "E12.4.4.5", {"start": v(-7.44, 12.4) * mm, "end": v(-8.94, 9.8) * mm});
            skCircle(sketch, "E12.4.4.6", {"center": v(-10.44, 12.4) * mm, "radius": 2.6 * mm, "construction": true});
            skPoint(sketch, "E12.4.4.7", {"position": v(-10.44, 15) * mm});
            skLineSegment(sketch, "E12.5.0.0", {"start": v(-4.44, 44.4) * mm, "end": v(-2.94, 47) * mm});
            skLineSegment(sketch, "E12.5.0.1", {"start": v(-2.94, 41.8) * mm, "end": v(-4.44, 44.4) * mm});
            skLineSegment(sketch, "E12.5.0.2", {"start": v(0.06, 47) * mm, "end": v(1.56, 44.4) * mm});
            skLineSegment(sketch, "E12.5.0.3", {"start": v(-2.94, 47) * mm, "end": v(0.06, 47) * mm});
            skLineSegment(sketch, "E12.5.0.4", {"start": v(0.06, 41.8) * mm, "end": v(-2.94, 41.8) * mm});
            skLineSegment(sketch, "E12.5.0.5", {"start": v(1.56, 44.4) * mm, "end": v(0.06, 41.8) * mm});
            skCircle(sketch, "E12.5.0.6", {"center": v(-1.44, 44.4) * mm, "radius": 2.6 * mm, "construction": true});
            skPoint(sketch, "E12.5.0.7", {"position": v(-1.44, 47) * mm});
            skLineSegment(sketch, "E12.5.1.0", {"start": v(-4.44, 36.4) * mm, "end": v(-2.94, 39) * mm});
            skLineSegment(sketch, "E12.5.1.1", {"start": v(-2.94, 33.8) * mm, "end": v(-4.44, 36.4) * mm});
            skLineSegment(sketch, "E12.5.1.2", {"start": v(0.06, 39) * mm, "end": v(1.56, 36.4) * mm});
            skLineSegment(sketch, "E12.5.1.3", {"start": v(-2.94, 39) * mm, "end": v(0.06, 39) * mm});
            skLineSegment(sketch, "E12.5.1.4", {"start": v(0.06, 33.8) * mm, "end": v(-2.94, 33.8) * mm});
            skLineSegment(sketch, "E12.5.1.5", {"start": v(1.56, 36.4) * mm, "end": v(0.06, 33.8) * mm});
            skCircle(sketch, "E12.5.1.6", {"center": v(-1.44, 36.4) * mm, "radius": 2.6 * mm, "construction": true});
            skPoint(sketch, "E12.5.1.7", {"position": v(-1.44, 39) * mm});
            skLineSegment(sketch, "E12.5.2.0", {"start": v(-4.44, 28.4) * mm, "end": v(-2.94, 31) * mm});
            skLineSegment(sketch, "E12.5.2.1", {"start": v(-2.94, 25.8) * mm, "end": v(-4.44, 28.4) * mm});
            skLineSegment(sketch, "E12.5.2.2", {"start": v(0.06, 31) * mm, "end": v(1.56, 28.4) * mm});
            skLineSegment(sketch, "E12.5.2.3", {"start": v(-2.94, 31) * mm, "end": v(0.06, 31) * mm});
            skLineSegment(sketch, "E12.5.2.4", {"start": v(0.06, 25.8) * mm, "end": v(-2.94, 25.8) * mm});
            skLineSegment(sketch, "E12.5.2.5", {"start": v(1.56, 28.4) * mm, "end": v(0.06, 25.8) * mm});
            skCircle(sketch, "E12.5.2.6", {"center": v(-1.44, 28.4) * mm, "radius": 2.6 * mm, "construction": true});
            skPoint(sketch, "E12.5.2.7", {"position": v(-1.44, 31) * mm});
            skLineSegment(sketch, "E12.5.3.0", {"start": v(-4.44, 20.4) * mm, "end": v(-2.94, 23) * mm});
            skLineSegment(sketch, "E12.5.3.1", {"start": v(-2.94, 17.8) * mm, "end": v(-4.44, 20.4) * mm});
            skLineSegment(sketch, "E12.5.3.2", {"start": v(0.06, 23) * mm, "end": v(1.56, 20.4) * mm});
            skLineSegment(sketch, "E12.5.3.3", {"start": v(-2.94, 23) * mm, "end": v(0.06, 23) * mm});
            skLineSegment(sketch, "E12.5.3.4", {"start": v(0.06, 17.8) * mm, "end": v(-2.94, 17.8) * mm});
            skLineSegment(sketch, "E12.5.3.5", {"start": v(1.56, 20.4) * mm, "end": v(0.06, 17.8) * mm});
            skCircle(sketch, "E12.5.3.6", {"center": v(-1.44, 20.4) * mm, "radius": 2.6 * mm, "construction": true});
            skPoint(sketch, "E12.5.3.7", {"position": v(-1.44, 23) * mm});
            skLineSegment(sketch, "E12.5.4.0", {"start": v(-4.44, 12.4) * mm, "end": v(-2.94, 15) * mm});
            skLineSegment(sketch, "E12.5.4.1", {"start": v(-2.94, 9.8) * mm, "end": v(-4.44, 12.4) * mm});
            skLineSegment(sketch, "E12.5.4.2", {"start": v(0.06, 15) * mm, "end": v(1.56, 12.4) * mm});
            skLineSegment(sketch, "E12.5.4.3", {"start": v(-2.94, 15) * mm, "end": v(0.06, 15) * mm});
            skLineSegment(sketch, "E12.5.4.4", {"start": v(0.06, 9.8) * mm, "end": v(-2.94, 9.8) * mm});
            skLineSegment(sketch, "E12.5.4.5", {"start": v(1.56, 12.4) * mm, "end": v(0.06, 9.8) * mm});
            skCircle(sketch, "E12.5.4.6", {"center": v(-1.44, 12.4) * mm, "radius": 2.6 * mm, "construction": true});
            skPoint(sketch, "E12.5.4.7", {"position": v(-1.44, 15) * mm});
            skLineSegment(sketch, "E12.6.0.0", {"start": v(4.56, 44.4) * mm, "end": v(6.06, 47) * mm});
            skLineSegment(sketch, "E12.6.0.1", {"start": v(6.06, 41.8) * mm, "end": v(4.56, 44.4) * mm});
            skLineSegment(sketch, "E12.6.0.2", {"start": v(9.06, 47) * mm, "end": v(10.56, 44.4) * mm});
            skLineSegment(sketch, "E12.6.0.3", {"start": v(6.06, 47) * mm, "end": v(9.06, 47) * mm});
            skLineSegment(sketch, "E12.6.0.4", {"start": v(9.06, 41.8) * mm, "end": v(6.06, 41.8) * mm});
            skLineSegment(sketch, "E12.6.0.5", {"start": v(10.56, 44.4) * mm, "end": v(9.06, 41.8) * mm});
            skCircle(sketch, "E12.6.0.6", {"center": v(7.56, 44.4) * mm, "radius": 2.6 * mm, "construction": true});
            skPoint(sketch, "E12.6.0.7", {"position": v(7.56, 47) * mm});
            skLineSegment(sketch, "E12.6.1.0", {"start": v(4.56, 36.4) * mm, "end": v(6.06, 39) * mm});
            skLineSegment(sketch, "E12.6.1.1", {"start": v(6.06, 33.8) * mm, "end": v(4.56, 36.4) * mm});
            skLineSegment(sketch, "E12.6.1.2", {"start": v(9.06, 39) * mm, "end": v(10.56, 36.4) * mm});
            skLineSegment(sketch, "E12.6.1.3", {"start": v(6.06, 39) * mm, "end": v(9.06, 39) * mm});
            skLineSegment(sketch, "E12.6.1.4", {"start": v(9.06, 33.8) * mm, "end": v(6.06, 33.8) * mm});
            skLineSegment(sketch, "E12.6.1.5", {"start": v(10.56, 36.4) * mm, "end": v(9.06, 33.8) * mm});
            skCircle(sketch, "E12.6.1.6", {"center": v(7.56, 36.4) * mm, "radius": 2.6 * mm, "construction": true});
            skPoint(sketch, "E12.6.1.7", {"position": v(7.56, 39) * mm});
            skLineSegment(sketch, "E12.6.2.0", {"start": v(4.56, 28.4) * mm, "end": v(6.06, 31) * mm});
            skLineSegment(sketch, "E12.6.2.1", {"start": v(6.06, 25.8) * mm, "end": v(4.56, 28.4) * mm});
            skLineSegment(sketch, "E12.6.2.2", {"start": v(9.06, 31) * mm, "end": v(10.56, 28.4) * mm});
            skLineSegment(sketch, "E12.6.2.3", {"start": v(6.06, 31) * mm, "end": v(9.06, 31) * mm});
            skLineSegment(sketch, "E12.6.2.4", {"start": v(9.06, 25.8) * mm, "end": v(6.06, 25.8) * mm});
            skLineSegment(sketch, "E12.6.2.5", {"start": v(10.56, 28.4) * mm, "end": v(9.06, 25.8) * mm});
            skCircle(sketch, "E12.6.2.6", {"center": v(7.56, 28.4) * mm, "radius": 2.6 * mm, "construction": true});
            skPoint(sketch, "E12.6.2.7", {"position": v(7.56, 31) * mm});
            skLineSegment(sketch, "E12.6.3.0", {"start": v(4.56, 20.4) * mm, "end": v(6.06, 23) * mm});
            skLineSegment(sketch, "E12.6.3.1", {"start": v(6.06, 17.8) * mm, "end": v(4.56, 20.4) * mm});
            skLineSegment(sketch, "E12.6.3.2", {"start": v(9.06, 23) * mm, "end": v(10.56, 20.4) * mm});
            skLineSegment(sketch, "E12.6.3.3", {"start": v(6.06, 23) * mm, "end": v(9.06, 23) * mm});
            skLineSegment(sketch, "E12.6.3.4", {"start": v(9.06, 17.8) * mm, "end": v(6.06, 17.8) * mm});
            skLineSegment(sketch, "E12.6.3.5", {"start": v(10.56, 20.4) * mm, "end": v(9.06, 17.8) * mm});
            skCircle(sketch, "E12.6.3.6", {"center": v(7.56, 20.4) * mm, "radius": 2.6 * mm, "construction": true});
            skPoint(sketch, "E12.6.3.7", {"position": v(7.56, 23) * mm});
            skLineSegment(sketch, "E12.6.4.0", {"start": v(4.56, 12.4) * mm, "end": v(6.06, 15) * mm});
            skLineSegment(sketch, "E12.6.4.1", {"start": v(6.06, 9.8) * mm, "end": v(4.56, 12.4) * mm});
            skLineSegment(sketch, "E12.6.4.2", {"start": v(9.06, 15) * mm, "end": v(10.56, 12.4) * mm});
            skLineSegment(sketch, "E12.6.4.3", {"start": v(6.06, 15) * mm, "end": v(9.06, 15) * mm});
            skLineSegment(sketch, "E12.6.4.4", {"start": v(9.06, 9.8) * mm, "end": v(6.06, 9.8) * mm});
            skLineSegment(sketch, "E12.6.4.5", {"start": v(10.56, 12.4) * mm, "end": v(9.06, 9.8) * mm});
            skCircle(sketch, "E12.6.4.6", {"center": v(7.56, 12.4) * mm, "radius": 2.6 * mm, "construction": true});
            skPoint(sketch, "E12.6.4.7", {"position": v(7.56, 15) * mm});
            skLineSegment(sketch, "E12.7.0.0", {"start": v(13.56, 44.4) * mm, "end": v(15.06, 47) * mm});
            skLineSegment(sketch, "E12.7.0.1", {"start": v(15.06, 41.8) * mm, "end": v(13.56, 44.4) * mm});
            skLineSegment(sketch, "E12.7.0.2", {"start": v(18.06, 47) * mm, "end": v(19.56, 44.4) * mm});
            skLineSegment(sketch, "E12.7.0.3", {"start": v(15.06, 47) * mm, "end": v(18.06, 47) * mm});
            skLineSegment(sketch, "E12.7.0.4", {"start": v(18.06, 41.8) * mm, "end": v(15.06, 41.8) * mm});
            skLineSegment(sketch, "E12.7.0.5", {"start": v(19.56, 44.4) * mm, "end": v(18.06, 41.8) * mm});
            skCircle(sketch, "E12.7.0.6", {"center": v(16.56, 44.4) * mm, "radius": 2.6 * mm, "construction": true});
            skPoint(sketch, "E12.7.0.7", {"position": v(16.56, 47) * mm});
            skLineSegment(sketch, "E12.7.1.0", {"start": v(13.56, 36.4) * mm, "end": v(15.06, 39) * mm});
            skLineSegment(sketch, "E12.7.1.1", {"start": v(15.06, 33.8) * mm, "end": v(13.56, 36.4) * mm});
            skLineSegment(sketch, "E12.7.1.2", {"start": v(18.06, 39) * mm, "end": v(19.56, 36.4) * mm});
            skLineSegment(sketch, "E12.7.1.3", {"start": v(15.06, 39) * mm, "end": v(18.06, 39) * mm});
            skLineSegment(sketch, "E12.7.1.4", {"start": v(18.06, 33.8) * mm, "end": v(15.06, 33.8) * mm});
            skLineSegment(sketch, "E12.7.1.5", {"start": v(19.56, 36.4) * mm, "end": v(18.06, 33.8) * mm});
            skCircle(sketch, "E12.7.1.6", {"center": v(16.56, 36.4) * mm, "radius": 2.6 * mm, "construction": true});
            skPoint(sketch, "E12.7.1.7", {"position": v(16.56, 39) * mm});
            skLineSegment(sketch, "E12.7.2.0", {"start": v(13.56, 28.4) * mm, "end": v(15.06, 31) * mm});
            skLineSegment(sketch, "E12.7.2.1", {"start": v(15.06, 25.8) * mm, "end": v(13.56, 28.4) * mm});
            skLineSegment(sketch, "E12.7.2.2", {"start": v(18.06, 31) * mm, "end": v(19.56, 28.4) * mm});
            skLineSegment(sketch, "E12.7.2.3", {"start": v(15.06, 31) * mm, "end": v(18.06, 31) * mm});
            skLineSegment(sketch, "E12.7.2.4", {"start": v(18.06, 25.8) * mm, "end": v(15.06, 25.8) * mm});
            skLineSegment(sketch, "E12.7.2.5", {"start": v(19.56, 28.4) * mm, "end": v(18.06, 25.8) * mm});
            skCircle(sketch, "E12.7.2.6", {"center": v(16.56, 28.4) * mm, "radius": 2.6 * mm, "construction": true});
            skPoint(sketch, "E12.7.2.7", {"position": v(16.56, 31) * mm});
            skLineSegment(sketch, "E12.7.3.0", {"start": v(13.56, 20.4) * mm, "end": v(15.06, 23) * mm});
            skLineSegment(sketch, "E12.7.3.1", {"start": v(15.06, 17.8) * mm, "end": v(13.56, 20.4) * mm});
            skLineSegment(sketch, "E12.7.3.2", {"start": v(18.06, 23) * mm, "end": v(19.56, 20.4) * mm});
            skLineSegment(sketch, "E12.7.3.3", {"start": v(15.06, 23) * mm, "end": v(18.06, 23) * mm});
            skLineSegment(sketch, "E12.7.3.4", {"start": v(18.06, 17.8) * mm, "end": v(15.06, 17.8) * mm});
            skLineSegment(sketch, "E12.7.3.5", {"start": v(19.56, 20.4) * mm, "end": v(18.06, 17.8) * mm});
            skCircle(sketch, "E12.7.3.6", {"center": v(16.56, 20.4) * mm, "radius": 2.6 * mm, "construction": true});
            skPoint(sketch, "E12.7.3.7", {"position": v(16.56, 23) * mm});
            skLineSegment(sketch, "E12.7.4.0", {"start": v(13.56, 12.4) * mm, "end": v(15.06, 15) * mm});
            skLineSegment(sketch, "E12.7.4.1", {"start": v(15.06, 9.8) * mm, "end": v(13.56, 12.4) * mm});
            skLineSegment(sketch, "E12.7.4.2", {"start": v(18.06, 15) * mm, "end": v(19.56, 12.4) * mm});
            skLineSegment(sketch, "E12.7.4.3", {"start": v(15.06, 15) * mm, "end": v(18.06, 15) * mm});
            skLineSegment(sketch, "E12.7.4.4", {"start": v(18.06, 9.8) * mm, "end": v(15.06, 9.8) * mm});
            skLineSegment(sketch, "E12.7.4.5", {"start": v(19.56, 12.4) * mm, "end": v(18.06, 9.8) * mm});
            skCircle(sketch, "E12.7.4.6", {"center": v(16.56, 12.4) * mm, "radius": 2.6 * mm, "construction": true});
            skPoint(sketch, "E12.7.4.7", {"position": v(16.56, 15) * mm});
            skLineSegment(sketch, "E12.8.0.0", {"start": v(22.56, 44.4) * mm, "end": v(24.06, 47) * mm});
            skLineSegment(sketch, "E12.8.0.1", {"start": v(24.06, 41.8) * mm, "end": v(22.56, 44.4) * mm});
            skLineSegment(sketch, "E12.8.0.2", {"start": v(27.06, 47) * mm, "end": v(28.56, 44.4) * mm});
            skLineSegment(sketch, "E12.8.0.3", {"start": v(24.06, 47) * mm, "end": v(27.06, 47) * mm});
            skLineSegment(sketch, "E12.8.0.4", {"start": v(27.06, 41.8) * mm, "end": v(24.06, 41.8) * mm});
            skLineSegment(sketch, "E12.8.0.5", {"start": v(28.56, 44.4) * mm, "end": v(27.06, 41.8) * mm});
            skCircle(sketch, "E12.8.0.6", {"center": v(25.56, 44.4) * mm, "radius": 2.6 * mm, "construction": true});
            skPoint(sketch, "E12.8.0.7", {"position": v(25.56, 47) * mm});
            skLineSegment(sketch, "E12.8.1.0", {"start": v(22.56, 36.4) * mm, "end": v(24.06, 39) * mm});
            skLineSegment(sketch, "E12.8.1.1", {"start": v(24.06, 33.8) * mm, "end": v(22.56, 36.4) * mm});
            skLineSegment(sketch, "E12.8.1.2", {"start": v(27.06, 39) * mm, "end": v(28.56, 36.4) * mm});
            skLineSegment(sketch, "E12.8.1.3", {"start": v(24.06, 39) * mm, "end": v(27.06, 39) * mm});
            skLineSegment(sketch, "E12.8.1.4", {"start": v(27.06, 33.8) * mm, "end": v(24.06, 33.8) * mm});
            skLineSegment(sketch, "E12.8.1.5", {"start": v(28.56, 36.4) * mm, "end": v(27.06, 33.8) * mm});
            skCircle(sketch, "E12.8.1.6", {"center": v(25.56, 36.4) * mm, "radius": 2.6 * mm, "construction": true});
            skPoint(sketch, "E12.8.1.7", {"position": v(25.56, 39) * mm});
            skLineSegment(sketch, "E12.8.2.0", {"start": v(22.56, 28.4) * mm, "end": v(24.06, 31) * mm});
            skLineSegment(sketch, "E12.8.2.1", {"start": v(24.06, 25.8) * mm, "end": v(22.56, 28.4) * mm});
            skLineSegment(sketch, "E12.8.2.2", {"start": v(27.06, 31) * mm, "end": v(28.56, 28.4) * mm});
            skLineSegment(sketch, "E12.8.2.3", {"start": v(24.06, 31) * mm, "end": v(27.06, 31) * mm});
            skLineSegment(sketch, "E12.8.2.4", {"start": v(27.06, 25.8) * mm, "end": v(24.06, 25.8) * mm});
            skLineSegment(sketch, "E12.8.2.5", {"start": v(28.56, 28.4) * mm, "end": v(27.06, 25.8) * mm});
            skCircle(sketch, "E12.8.2.6", {"center": v(25.56, 28.4) * mm, "radius": 2.6 * mm, "construction": true});
            skPoint(sketch, "E12.8.2.7", {"position": v(25.56, 31) * mm});
            skLineSegment(sketch, "E12.8.3.0", {"start": v(22.56, 20.4) * mm, "end": v(24.06, 23) * mm});
            skLineSegment(sketch, "E12.8.3.1", {"start": v(24.06, 17.8) * mm, "end": v(22.56, 20.4) * mm});
            skLineSegment(sketch, "E12.8.3.2", {"start": v(27.06, 23) * mm, "end": v(28.56, 20.4) * mm});
            skLineSegment(sketch, "E12.8.3.3", {"start": v(24.06, 23) * mm, "end": v(27.06, 23) * mm});
            skLineSegment(sketch, "E12.8.3.4", {"start": v(27.06, 17.8) * mm, "end": v(24.06, 17.8) * mm});
            skLineSegment(sketch, "E12.8.3.5", {"start": v(28.56, 20.4) * mm, "end": v(27.06, 17.8) * mm});
            skCircle(sketch, "E12.8.3.6", {"center": v(25.56, 20.4) * mm, "radius": 2.6 * mm, "construction": true});
            skPoint(sketch, "E12.8.3.7", {"position": v(25.56, 23) * mm});
            skLineSegment(sketch, "E12.8.4.0", {"start": v(22.56, 12.4) * mm, "end": v(24.06, 15) * mm});
            skLineSegment(sketch, "E12.8.4.1", {"start": v(24.06, 9.8) * mm, "end": v(22.56, 12.4) * mm});
            skLineSegment(sketch, "E12.8.4.2", {"start": v(27.06, 15) * mm, "end": v(28.56, 12.4) * mm});
            skLineSegment(sketch, "E12.8.4.3", {"start": v(24.06, 15) * mm, "end": v(27.06, 15) * mm});
            skLineSegment(sketch, "E12.8.4.4", {"start": v(27.06, 9.8) * mm, "end": v(24.06, 9.8) * mm});
            skLineSegment(sketch, "E12.8.4.5", {"start": v(28.56, 12.4) * mm, "end": v(27.06, 9.8) * mm});
            skCircle(sketch, "E12.8.4.6", {"center": v(25.56, 12.4) * mm, "radius": 2.6 * mm, "construction": true});
            skPoint(sketch, "E12.8.4.7", {"position": v(25.56, 15) * mm});
            skLineSegment(sketch, "E12.9.0.0", {"start": v(31.56, 44.4) * mm, "end": v(33.06, 47) * mm});
            skLineSegment(sketch, "E12.9.0.1", {"start": v(33.06, 41.8) * mm, "end": v(31.56, 44.4) * mm});
            skLineSegment(sketch, "E12.9.0.2", {"start": v(36.06, 47) * mm, "end": v(37.56, 44.4) * mm});
            skLineSegment(sketch, "E12.9.0.3", {"start": v(33.06, 47) * mm, "end": v(36.06, 47) * mm});
            skLineSegment(sketch, "E12.9.0.4", {"start": v(36.06, 41.8) * mm, "end": v(33.06, 41.8) * mm});
            skLineSegment(sketch, "E12.9.0.5", {"start": v(37.56, 44.4) * mm, "end": v(36.06, 41.8) * mm});
            skCircle(sketch, "E12.9.0.6", {"center": v(34.56, 44.4) * mm, "radius": 2.6 * mm, "construction": true});
            skPoint(sketch, "E12.9.0.7", {"position": v(34.56, 47) * mm});
            skLineSegment(sketch, "E12.9.1.0", {"start": v(31.56, 36.4) * mm, "end": v(33.06, 39) * mm});
            skLineSegment(sketch, "E12.9.1.1", {"start": v(33.06, 33.8) * mm, "end": v(31.56, 36.4) * mm});
            skLineSegment(sketch, "E12.9.1.2", {"start": v(36.06, 39) * mm, "end": v(37.56, 36.4) * mm});
            skLineSegment(sketch, "E12.9.1.3", {"start": v(33.06, 39) * mm, "end": v(36.06, 39) * mm});
            skLineSegment(sketch, "E12.9.1.4", {"start": v(36.06, 33.8) * mm, "end": v(33.06, 33.8) * mm});
            skLineSegment(sketch, "E12.9.1.5", {"start": v(37.56, 36.4) * mm, "end": v(36.06, 33.8) * mm});
            skCircle(sketch, "E12.9.1.6", {"center": v(34.56, 36.4) * mm, "radius": 2.6 * mm, "construction": true});
            skPoint(sketch, "E12.9.1.7", {"position": v(34.56, 39) * mm});
            skLineSegment(sketch, "E12.9.2.0", {"start": v(31.56, 28.4) * mm, "end": v(33.06, 31) * mm});
            skLineSegment(sketch, "E12.9.2.1", {"start": v(33.06, 25.8) * mm, "end": v(31.56, 28.4) * mm});
            skLineSegment(sketch, "E12.9.2.2", {"start": v(36.06, 31) * mm, "end": v(37.56, 28.4) * mm});
            skLineSegment(sketch, "E12.9.2.3", {"start": v(33.06, 31) * mm, "end": v(36.06, 31) * mm});
            skLineSegment(sketch, "E12.9.2.4", {"start": v(36.06, 25.8) * mm, "end": v(33.06, 25.8) * mm});
            skLineSegment(sketch, "E12.9.2.5", {"start": v(37.56, 28.4) * mm, "end": v(36.06, 25.8) * mm});
            skCircle(sketch, "E12.9.2.6", {"center": v(34.56, 28.4) * mm, "radius": 2.6 * mm, "construction": true});
            skPoint(sketch, "E12.9.2.7", {"position": v(34.56, 31) * mm});
            skLineSegment(sketch, "E12.9.3.0", {"start": v(31.56, 20.4) * mm, "end": v(33.06, 23) * mm});
            skLineSegment(sketch, "E12.9.3.1", {"start": v(33.06, 17.8) * mm, "end": v(31.56, 20.4) * mm});
            skLineSegment(sketch, "E12.9.3.2", {"start": v(36.06, 23) * mm, "end": v(37.56, 20.4) * mm});
            skLineSegment(sketch, "E12.9.3.3", {"start": v(33.06, 23) * mm, "end": v(36.06, 23) * mm});
            skLineSegment(sketch, "E12.9.3.4", {"start": v(36.06, 17.8) * mm, "end": v(33.06, 17.8) * mm});
            skLineSegment(sketch, "E12.9.3.5", {"start": v(37.56, 20.4) * mm, "end": v(36.06, 17.8) * mm});
            skCircle(sketch, "E12.9.3.6", {"center": v(34.56, 20.4) * mm, "radius": 2.6 * mm, "construction": true});
            skPoint(sketch, "E12.9.3.7", {"position": v(34.56, 23) * mm});
            skLineSegment(sketch, "E12.9.4.0", {"start": v(31.56, 12.4) * mm, "end": v(33.06, 15) * mm});
            skLineSegment(sketch, "E12.9.4.1", {"start": v(33.06, 9.8) * mm, "end": v(31.56, 12.4) * mm});
            skLineSegment(sketch, "E12.9.4.2", {"start": v(36.06, 15) * mm, "end": v(37.56, 12.4) * mm});
            skLineSegment(sketch, "E12.9.4.3", {"start": v(33.06, 15) * mm, "end": v(36.06, 15) * mm});
            skLineSegment(sketch, "E12.9.4.4", {"start": v(36.06, 9.8) * mm, "end": v(33.06, 9.8) * mm});
            skLineSegment(sketch, "E12.9.4.5", {"start": v(37.56, 12.4) * mm, "end": v(36.06, 9.8) * mm});
            skCircle(sketch, "E12.9.4.6", {"center": v(34.56, 12.4) * mm, "radius": 2.6 * mm, "construction": true});
            skPoint(sketch, "E12.9.4.7", {"position": v(34.56, 15) * mm});
            skLineSegment(sketch, "E12.10.0.0", {"start": v(40.56, 44.4) * mm, "end": v(42.06, 47) * mm});
            skLineSegment(sketch, "E12.10.0.1", {"start": v(42.06, 41.8) * mm, "end": v(40.56, 44.4) * mm});
            skLineSegment(sketch, "E12.10.0.2", {"start": v(45.06, 47) * mm, "end": v(46.56, 44.4) * mm});
            skLineSegment(sketch, "E12.10.0.3", {"start": v(42.06, 47) * mm, "end": v(45.06, 47) * mm});
            skLineSegment(sketch, "E12.10.0.4", {"start": v(45.06, 41.8) * mm, "end": v(42.06, 41.8) * mm});
            skLineSegment(sketch, "E12.10.0.5", {"start": v(46.56, 44.4) * mm, "end": v(45.06, 41.8) * mm});
            skCircle(sketch, "E12.10.0.6", {"center": v(43.56, 44.4) * mm, "radius": 2.6 * mm, "construction": true});
            skPoint(sketch, "E12.10.0.7", {"position": v(43.56, 47) * mm});
            skLineSegment(sketch, "E12.10.1.0", {"start": v(40.56, 36.4) * mm, "end": v(42.06, 39) * mm});
            skLineSegment(sketch, "E12.10.1.1", {"start": v(42.06, 33.8) * mm, "end": v(40.56, 36.4) * mm});
            skLineSegment(sketch, "E12.10.1.2", {"start": v(45.06, 39) * mm, "end": v(46.56, 36.4) * mm});
            skLineSegment(sketch, "E12.10.1.3", {"start": v(42.06, 39) * mm, "end": v(45.06, 39) * mm});
            skLineSegment(sketch, "E12.10.1.4", {"start": v(45.06, 33.8) * mm, "end": v(42.06, 33.8) * mm});
            skLineSegment(sketch, "E12.10.1.5", {"start": v(46.56, 36.4) * mm, "end": v(45.06, 33.8) * mm});
            skCircle(sketch, "E12.10.1.6", {"center": v(43.56, 36.4) * mm, "radius": 2.6 * mm, "construction": true});
            skPoint(sketch, "E12.10.1.7", {"position": v(43.56, 39) * mm});
            skLineSegment(sketch, "E12.10.2.0", {"start": v(40.56, 28.4) * mm, "end": v(42.06, 31) * mm});
            skLineSegment(sketch, "E12.10.2.1", {"start": v(42.06, 25.8) * mm, "end": v(40.56, 28.4) * mm});
            skLineSegment(sketch, "E12.10.2.2", {"start": v(45.06, 31) * mm, "end": v(46.56, 28.4) * mm});
            skLineSegment(sketch, "E12.10.2.3", {"start": v(42.06, 31) * mm, "end": v(45.06, 31) * mm});
            skLineSegment(sketch, "E12.10.2.4", {"start": v(45.06, 25.8) * mm, "end": v(42.06, 25.8) * mm});
            skLineSegment(sketch, "E12.10.2.5", {"start": v(46.56, 28.4) * mm, "end": v(45.06, 25.8) * mm});
            skCircle(sketch, "E12.10.2.6", {"center": v(43.56, 28.4) * mm, "radius": 2.6 * mm, "construction": true});
            skPoint(sketch, "E12.10.2.7", {"position": v(43.56, 31) * mm});
            skLineSegment(sketch, "E12.10.3.0", {"start": v(40.56, 20.4) * mm, "end": v(42.06, 23) * mm});
            skLineSegment(sketch, "E12.10.3.1", {"start": v(42.06, 17.8) * mm, "end": v(40.56, 20.4) * mm});
            skLineSegment(sketch, "E12.10.3.2", {"start": v(45.06, 23) * mm, "end": v(46.56, 20.4) * mm});
            skLineSegment(sketch, "E12.10.3.3", {"start": v(42.06, 23) * mm, "end": v(45.06, 23) * mm});
            skLineSegment(sketch, "E12.10.3.4", {"start": v(45.06, 17.8) * mm, "end": v(42.06, 17.8) * mm});
            skLineSegment(sketch, "E12.10.3.5", {"start": v(46.56, 20.4) * mm, "end": v(45.06, 17.8) * mm});
            skCircle(sketch, "E12.10.3.6", {"center": v(43.56, 20.4) * mm, "radius": 2.6 * mm, "construction": true});
            skPoint(sketch, "E12.10.3.7", {"position": v(43.56, 23) * mm});
            skLineSegment(sketch, "E12.10.4.0", {"start": v(40.56, 12.4) * mm, "end": v(42.06, 15) * mm});
            skLineSegment(sketch, "E12.10.4.1", {"start": v(42.06, 9.8) * mm, "end": v(40.56, 12.4) * mm});
            skLineSegment(sketch, "E12.10.4.2", {"start": v(45.06, 15) * mm, "end": v(46.56, 12.4) * mm});
            skLineSegment(sketch, "E12.10.4.3", {"start": v(42.06, 15) * mm, "end": v(45.06, 15) * mm});
            skLineSegment(sketch, "E12.10.4.4", {"start": v(45.06, 9.8) * mm, "end": v(42.06, 9.8) * mm});
            skLineSegment(sketch, "E12.10.4.5", {"start": v(46.56, 12.4) * mm, "end": v(45.06, 9.8) * mm});
            skCircle(sketch, "E12.10.4.6", {"center": v(43.56, 12.4) * mm, "radius": 2.6 * mm, "construction": true});
            skPoint(sketch, "E12.10.4.7", {"position": v(43.56, 15) * mm});
            skLineSegment(sketch, "E12.11.0.0", {"start": v(49.56, 44.4) * mm, "end": v(51.06, 47) * mm});
            skLineSegment(sketch, "E12.11.0.1", {"start": v(51.06, 41.8) * mm, "end": v(49.56, 44.4) * mm});
            skLineSegment(sketch, "E12.11.0.2", {"start": v(54.06, 47) * mm, "end": v(55.56, 44.4) * mm});
            skLineSegment(sketch, "E12.11.0.3", {"start": v(51.06, 47) * mm, "end": v(54.06, 47) * mm});
            skLineSegment(sketch, "E12.11.0.4", {"start": v(54.06, 41.8) * mm, "end": v(51.06, 41.8) * mm});
            skLineSegment(sketch, "E12.11.0.5", {"start": v(55.56, 44.4) * mm, "end": v(54.06, 41.8) * mm});
            skCircle(sketch, "E12.11.0.6", {"center": v(52.56, 44.4) * mm, "radius": 2.6 * mm, "construction": true});
            skPoint(sketch, "E12.11.0.7", {"position": v(52.56, 47) * mm});
            skLineSegment(sketch, "E12.11.1.0", {"start": v(49.56, 36.4) * mm, "end": v(51.06, 39) * mm});
            skLineSegment(sketch, "E12.11.1.1", {"start": v(51.06, 33.8) * mm, "end": v(49.56, 36.4) * mm});
            skLineSegment(sketch, "E12.11.1.2", {"start": v(54.06, 39) * mm, "end": v(55.56, 36.4) * mm});
            skLineSegment(sketch, "E12.11.1.3", {"start": v(51.06, 39) * mm, "end": v(54.06, 39) * mm});
            skLineSegment(sketch, "E12.11.1.4", {"start": v(54.06, 33.8) * mm, "end": v(51.06, 33.8) * mm});
            skLineSegment(sketch, "E12.11.1.5", {"start": v(55.56, 36.4) * mm, "end": v(54.06, 33.8) * mm});
            skCircle(sketch, "E12.11.1.6", {"center": v(52.56, 36.4) * mm, "radius": 2.6 * mm, "construction": true});
            skPoint(sketch, "E12.11.1.7", {"position": v(52.56, 39) * mm});
            skLineSegment(sketch, "E12.11.2.0", {"start": v(49.56, 28.4) * mm, "end": v(51.06, 31) * mm});
            skLineSegment(sketch, "E12.11.2.1", {"start": v(51.06, 25.8) * mm, "end": v(49.56, 28.4) * mm});
            skLineSegment(sketch, "E12.11.2.2", {"start": v(54.06, 31) * mm, "end": v(55.56, 28.4) * mm});
            skLineSegment(sketch, "E12.11.2.3", {"start": v(51.06, 31) * mm, "end": v(54.06, 31) * mm});
            skLineSegment(sketch, "E12.11.2.4", {"start": v(54.06, 25.8) * mm, "end": v(51.06, 25.8) * mm});
            skLineSegment(sketch, "E12.11.2.5", {"start": v(55.56, 28.4) * mm, "end": v(54.06, 25.8) * mm});
            skCircle(sketch, "E12.11.2.6", {"center": v(52.56, 28.4) * mm, "radius": 2.6 * mm, "construction": true});
            skPoint(sketch, "E12.11.2.7", {"position": v(52.56, 31) * mm});
            skLineSegment(sketch, "E12.11.3.0", {"start": v(49.56, 20.4) * mm, "end": v(51.06, 23) * mm});
            skLineSegment(sketch, "E12.11.3.1", {"start": v(51.06, 17.8) * mm, "end": v(49.56, 20.4) * mm});
            skLineSegment(sketch, "E12.11.3.2", {"start": v(54.06, 23) * mm, "end": v(55.56, 20.4) * mm});
            skLineSegment(sketch, "E12.11.3.3", {"start": v(51.06, 23) * mm, "end": v(54.06, 23) * mm});
            skLineSegment(sketch, "E12.11.3.4", {"start": v(54.06, 17.8) * mm, "end": v(51.06, 17.8) * mm});
            skLineSegment(sketch, "E12.11.3.5", {"start": v(55.56, 20.4) * mm, "end": v(54.06, 17.8) * mm});
            skCircle(sketch, "E12.11.3.6", {"center": v(52.56, 20.4) * mm, "radius": 2.6 * mm, "construction": true});
            skPoint(sketch, "E12.11.3.7", {"position": v(52.56, 23) * mm});
            skLineSegment(sketch, "E12.11.4.0", {"start": v(49.56, 12.4) * mm, "end": v(51.06, 15) * mm});
            skLineSegment(sketch, "E12.11.4.1", {"start": v(51.06, 9.8) * mm, "end": v(49.56, 12.4) * mm});
            skLineSegment(sketch, "E12.11.4.2", {"start": v(54.06, 15) * mm, "end": v(55.56, 12.4) * mm});
            skLineSegment(sketch, "E12.11.4.3", {"start": v(51.06, 15) * mm, "end": v(54.06, 15) * mm});
            skLineSegment(sketch, "E12.11.4.4", {"start": v(54.06, 9.8) * mm, "end": v(51.06, 9.8) * mm});
            skLineSegment(sketch, "E12.11.4.5", {"start": v(55.56, 12.4) * mm, "end": v(54.06, 9.8) * mm});
            skCircle(sketch, "E12.11.4.6", {"center": v(52.56, 12.4) * mm, "radius": 2.6 * mm, "construction": true});
            skPoint(sketch, "E12.11.4.7", {"position": v(52.56, 15) * mm});
            skLineSegment(sketch, "E12.12.0.0", {"start": v(58.56, 44.4) * mm, "end": v(60.06, 47) * mm});
            skLineSegment(sketch, "E12.12.0.1", {"start": v(60.06, 41.8) * mm, "end": v(58.56, 44.4) * mm});
            skLineSegment(sketch, "E12.12.0.2", {"start": v(63.06, 47) * mm, "end": v(64.56, 44.4) * mm});
            skLineSegment(sketch, "E12.12.0.3", {"start": v(60.06, 47) * mm, "end": v(63.06, 47) * mm});
            skLineSegment(sketch, "E12.12.0.4", {"start": v(63.06, 41.8) * mm, "end": v(60.06, 41.8) * mm});
            skLineSegment(sketch, "E12.12.0.5", {"start": v(64.56, 44.4) * mm, "end": v(63.06, 41.8) * mm});
            skCircle(sketch, "E12.12.0.6", {"center": v(61.56, 44.4) * mm, "radius": 2.6 * mm, "construction": true});
            skPoint(sketch, "E12.12.0.7", {"position": v(61.56, 47) * mm});
            skLineSegment(sketch, "E12.12.1.0", {"start": v(58.56, 36.4) * mm, "end": v(60.06, 39) * mm});
            skLineSegment(sketch, "E12.12.1.1", {"start": v(60.06, 33.8) * mm, "end": v(58.56, 36.4) * mm});
            skLineSegment(sketch, "E12.12.1.2", {"start": v(63.06, 39) * mm, "end": v(64.56, 36.4) * mm});
            skLineSegment(sketch, "E12.12.1.3", {"start": v(60.06, 39) * mm, "end": v(63.06, 39) * mm});
            skLineSegment(sketch, "E12.12.1.4", {"start": v(63.06, 33.8) * mm, "end": v(60.06, 33.8) * mm});
            skLineSegment(sketch, "E12.12.1.5", {"start": v(64.56, 36.4) * mm, "end": v(63.06, 33.8) * mm});
            skCircle(sketch, "E12.12.1.6", {"center": v(61.56, 36.4) * mm, "radius": 2.6 * mm, "construction": true});
            skPoint(sketch, "E12.12.1.7", {"position": v(61.56, 39) * mm});
            skLineSegment(sketch, "E12.12.2.0", {"start": v(58.56, 28.4) * mm, "end": v(60.06, 31) * mm});
            skLineSegment(sketch, "E12.12.2.1", {"start": v(60.06, 25.8) * mm, "end": v(58.56, 28.4) * mm});
            skLineSegment(sketch, "E12.12.2.2", {"start": v(63.06, 31) * mm, "end": v(64.56, 28.4) * mm});
            skLineSegment(sketch, "E12.12.2.3", {"start": v(60.06, 31) * mm, "end": v(63.06, 31) * mm});
            skLineSegment(sketch, "E12.12.2.4", {"start": v(63.06, 25.8) * mm, "end": v(60.06, 25.8) * mm});
            skLineSegment(sketch, "E12.12.2.5", {"start": v(64.56, 28.4) * mm, "end": v(63.06, 25.8) * mm});
            skCircle(sketch, "E12.12.2.6", {"center": v(61.56, 28.4) * mm, "radius": 2.6 * mm, "construction": true});
            skPoint(sketch, "E12.12.2.7", {"position": v(61.56, 31) * mm});
            skLineSegment(sketch, "E12.12.3.0", {"start": v(58.56, 20.4) * mm, "end": v(60.06, 23) * mm});
            skLineSegment(sketch, "E12.12.3.1", {"start": v(60.06, 17.8) * mm, "end": v(58.56, 20.4) * mm});
            skLineSegment(sketch, "E12.12.3.2", {"start": v(63.06, 23) * mm, "end": v(64.56, 20.4) * mm});
            skLineSegment(sketch, "E12.12.3.3", {"start": v(60.06, 23) * mm, "end": v(63.06, 23) * mm});
            skLineSegment(sketch, "E12.12.3.4", {"start": v(63.06, 17.8) * mm, "end": v(60.06, 17.8) * mm});
            skLineSegment(sketch, "E12.12.3.5", {"start": v(64.56, 20.4) * mm, "end": v(63.06, 17.8) * mm});
            skCircle(sketch, "E12.12.3.6", {"center": v(61.56, 20.4) * mm, "radius": 2.6 * mm, "construction": true});
            skPoint(sketch, "E12.12.3.7", {"position": v(61.56, 23) * mm});
            skLineSegment(sketch, "E12.12.4.0", {"start": v(58.56, 12.4) * mm, "end": v(60.06, 15) * mm});
            skLineSegment(sketch, "E12.12.4.1", {"start": v(60.06, 9.8) * mm, "end": v(58.56, 12.4) * mm});
            skLineSegment(sketch, "E12.12.4.2", {"start": v(63.06, 15) * mm, "end": v(64.56, 12.4) * mm});
            skLineSegment(sketch, "E12.12.4.3", {"start": v(60.06, 15) * mm, "end": v(63.06, 15) * mm});
            skLineSegment(sketch, "E12.12.4.4", {"start": v(63.06, 9.8) * mm, "end": v(60.06, 9.8) * mm});
            skLineSegment(sketch, "E12.12.4.5", {"start": v(64.56, 12.4) * mm, "end": v(63.06, 9.8) * mm});
            skCircle(sketch, "E12.12.4.6", {"center": v(61.56, 12.4) * mm, "radius": 2.6 * mm, "construction": true});
            skPoint(sketch, "E12.12.4.7", {"position": v(61.56, 15) * mm});
            skLineSegment(sketch, "E12.direction1", {"start": v(-46.44, 44.4) * mm, "end": v(-37.44, 44.4) * mm, "construction": true});
            skLineSegment(sketch, "E12.direction2", {"start": v(-46.44, 44.4) * mm, "end": v(-46.44, 36.4) * mm, "construction": true});
            skSolve(sketch);
        }
        {
            var Q0;
            Q0 = qSketchRegion(id + "F5", true);
            extrude(context, id + "F6", {"entities" : qUnion([Q0]), "operationType" : NewBodyOperationType.REMOVE, "endBound" : BoundingType.SYMMETRIC, "oppositeDirection" : true, "depth" : 100 * mm});
        }
    });
